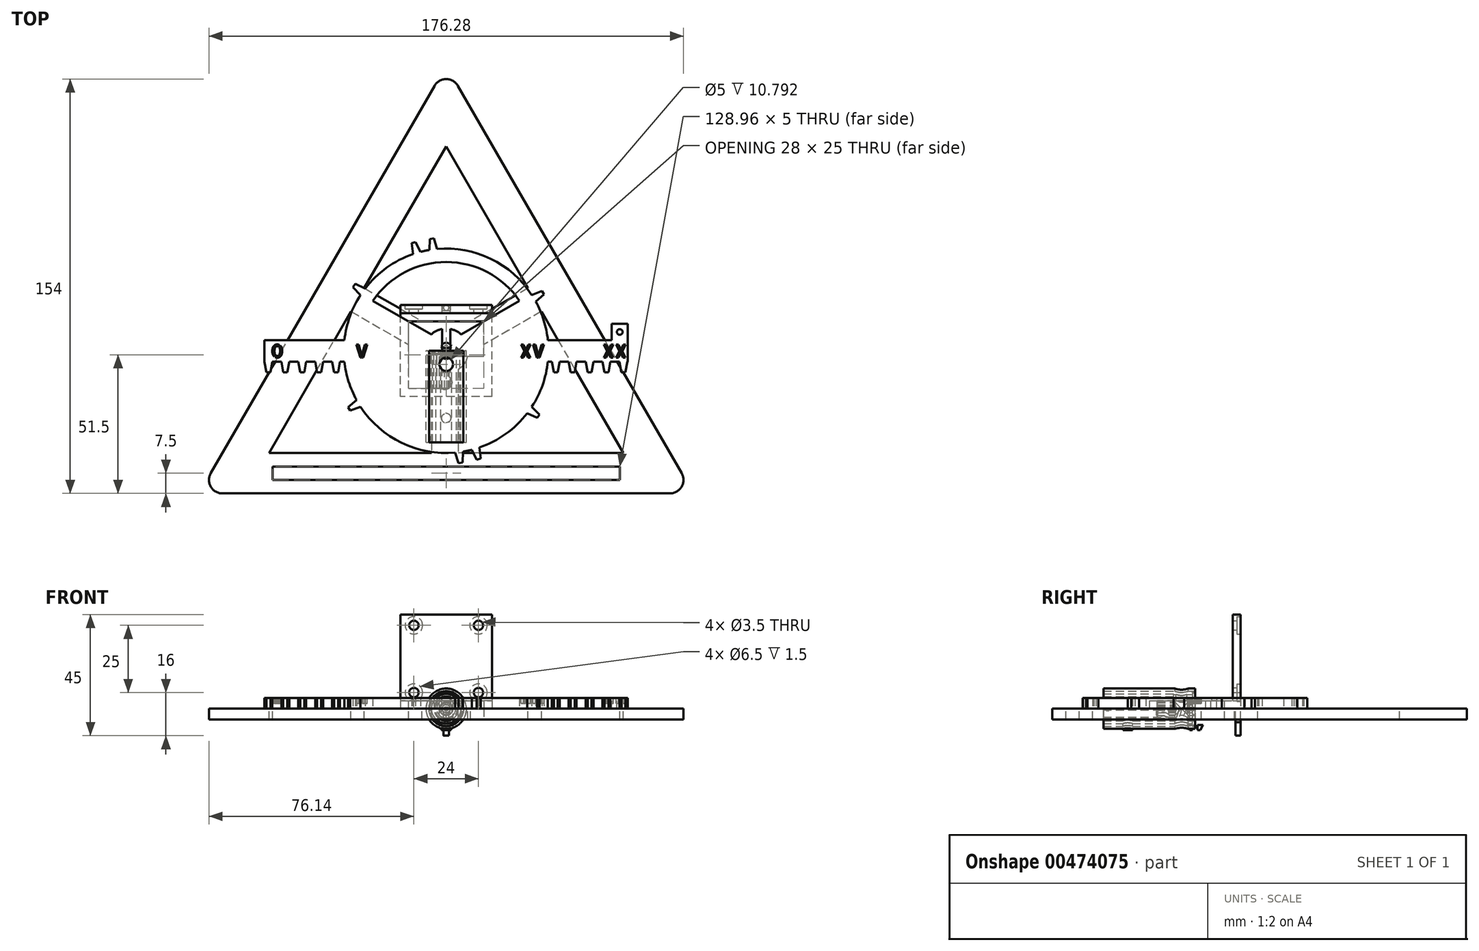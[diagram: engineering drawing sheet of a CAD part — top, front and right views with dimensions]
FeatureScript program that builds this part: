
annotation { "Feature Type Name" : "Feature", "Feature Type Description" : "" }
export const myFeature = defineFeature(function(context is Context, id is Id, definition is map)
    precondition{}
    {
        {
            var Q0;
            Q0=qCreatedBy(makeId("Top.planeOp"),FACE);
            var sketch = newSketch(context, id + "F0", { "sketchPlane" : qUnion([Q0])});
            skCircle(sketch, "E0.cCircle", {"center": v(0, 0) * mm, "radius": 53 * mm, "construction": true});
            skLineSegment(sketch, "E0.0", {"start": v(0, 106) * mm, "end": v(91.8, -53) * mm});
            skLineSegment(sketch, "E0.1", {"start": v(91.8, -53) * mm, "end": v(-91.8, -53) * mm});
            skLineSegment(sketch, "E0.2", {"start": v(-91.8, -53) * mm, "end": v(0, 106) * mm});
            skLineSegment(sketch, "E1.0", {"start": v(-83.14, -48) * mm, "end": v(0, 96) * mm});
            skLineSegment(sketch, "E1.1", {"start": v(83.14, -48) * mm, "end": v(-83.14, -48) * mm});
            skLineSegment(sketch, "E1.2", {"start": v(0, 96) * mm, "end": v(83.14, -48) * mm});
            skLineSegment(sketch, "E2.0", {"start": v(-74.48, -43) * mm, "end": v(0, 86) * mm});
            skLineSegment(sketch, "E2.1", {"start": v(74.48, -43) * mm, "end": v(-74.48, -43) * mm});
            skLineSegment(sketch, "E2.2", {"start": v(0, 86) * mm, "end": v(74.48, -43) * mm});
            skLineSegment(sketch, "E3.left", {"start": v(-64.48, -43) * mm, "end": v(-64.48, -48) * mm});
            skLineSegment(sketch, "E3.right", {"start": v(64.48, -48) * mm, "end": v(64.48, -50) * mm});
            skLineSegment(sketch, "E4", {"start": v(-69.48, -34.34) * mm, "end": v(-73.8, -31.84) * mm});
            skLineSegment(sketch, "E5", {"start": v(-5, 77.34) * mm, "end": v(-9.33, 79.84) * mm});
            skLineSegment(sketch, "E6", {"start": v(5.77, 76) * mm, "end": v(10.1, 78.5) * mm});
            skLineSegment(sketch, "E7", {"start": v(68.7, -33) * mm, "end": v(73.03, -30.5) * mm});
            skLineSegment(sketch, "E8", {"start": v(-37.24, 21.5) * mm, "end": v(-0.48, 0.28) * mm, "construction": true});
            skLineSegment(sketch, "E9", {"start": v(37.24, 21.5) * mm, "end": v(0, 0) * mm});
            skLineSegment(sketch, "E10", {"start": v(-0.48, 0.28) * mm, "end": v(-0.48, -43.46) * mm, "construction": true});
            skLineSegment(sketch, "E11.0", {"start": v(-5.48, -0.46) * mm, "end": v(-5.48, -43.46) * mm});
            skLineSegment(sketch, "E12.0", {"start": v(4.52, -0.46) * mm, "end": v(4.52, -43) * mm});
            skLineSegment(sketch, "E13.0", {"start": v(39.74, 17.17) * mm, "end": v(2.5, -4.33) * mm});
            skLineSegment(sketch, "E14.0", {"start": v(-39.74, 17.17) * mm, "end": v(-2.5, -4.33) * mm});
            skLineSegment(sketch, "E15.0", {"start": v(-34.74, 25.83) * mm, "end": v(2.5, 4.33) * mm});
            skLineSegment(sketch, "E16.0", {"start": v(65.82, -38) * mm, "end": v(-65.82, -38) * mm});
            skLineSegment(sketch, "E16.1", {"start": v(0, 76) * mm, "end": v(65.82, -38) * mm});
            skLineSegment(sketch, "E16.2", {"start": v(-65.82, -38) * mm, "end": v(0, 76) * mm});
            skLineSegment(sketch, "E17", {"start": v(64.48, -50) * mm, "end": v(64.48, -43) * mm});
            skCircle(sketch, "E18", {"center": v(10.14, 5.86) * mm, "radius": 2.6 * mm});
            skCircle(sketch, "E19", {"center": v(-10.87, 6.28) * mm, "radius": 2.6 * mm});
            skCircle(sketch, "E20", {"center": v(-0.48, -11.72) * mm, "radius": 2.6 * mm});
            skCircle(sketch, "E21", {"center": v(0, 0) * mm, "radius": 3.25 * mm});
            skPoint(sketch, "E22", {"position": v(8.18, -1.05) * mm});
            skPoint(sketch, "E23", {"position": v(4.52, -6.9) * mm});
            skPoint(sketch, "E24", {"position": v(2.67, 7.8) * mm});
            skPoint(sketch, "E25", {"position": v(-3.18, 7.61) * mm});
            skPoint(sketch, "E26", {"position": v(-8.18, -1.05) * mm});
            skPoint(sketch, "E27", {"position": v(-5.48, -6.9) * mm});
            skArc(sketch, "E28", {"start": v(8.18, -1.05) * mm, "mid": v(5.21, 6.4) * mm, "end": v(-2.68, 7.8) * mm});
            skArc(sketch, "E29", {"start": v(4.52, -6.9) * mm, "mid": v(7, -4.38) * mm, "end": v(8.18, -1.05) * mm});
            skArc(sketch, "E30", {"start": v(-2.68, 7.8) * mm, "mid": v(-7, 4.35) * mm, "end": v(-8.18, -1.05) * mm});
            skArc(sketch, "E31", {"start": v(-8.18, -1.05) * mm, "mid": v(-7.3, -3.85) * mm, "end": v(-5.48, -6.16) * mm});
            skArc(sketch, "E32", {"start": v(-5.48, -6.16) * mm, "mid": v(-0.6, -8.23) * mm, "end": v(4.52, -6.9) * mm});
            skLineSegment(sketch, "E33.0", {"start": v(34.74, 25.83) * mm, "end": v(-2.5, 4.33) * mm});
            skSolve(sketch);
        }
        {
            var Q0;
            {var subQ0=sQuery(id+"F0.wireOp",EDGE,"E2.2");var subQ1=sQuery(id+"F0.wireOp",EDGE,"E2.1");var subQ2=makeQuery(id+"F0.imprint","INTERSECT",VERTEX,{"derivedFrom":[subQ1,subQ0]});Q0=makeQuery(id+"F0.imprint","IMPRINT",FACE,{"disambiguationData":[TD([[makeQuery(id+"F0.imprint","IMPRINT",EDGE,{"disambiguationData":[TD([[subQ2,-1.0]])],"derivedFrom":subQ1}),-1.0]])]});}
            var Q1;
            Q1=makeQuery(id+"F0.imprint","IMPRINT",FACE,{"disambiguationData":[TD([[makeQuery(id+"F0.imprint","IMPRINT",EDGE,{"derivedFrom":sQuery(id+"F0.wireOp",EDGE,"E0.0")}),-1.0]])]});
            var Q2;
            {var subQ4=sQuery(id+"F0.wireOp",EDGE,"E2.0");var subQ6=makeQuery(id+"F0.imprint","INTERSECT",VERTEX,{"derivedFrom":[subQ4,sQuery(id+"F0.wireOp",EDGE,"E5")]});Q2=makeQuery(id+"F0.imprint","IMPRINT",FACE,{"disambiguationData":[TD([[makeQuery(id+"F0.imprint","IMPRINT",EDGE,{"disambiguationData":[TD([[subQ6,1.0]])],"derivedFrom":subQ4}),-1.0]])]});}
            var Q3;
            {var subQ0=sQuery(id+"F0.wireOp",EDGE,"E2.1");var subQ1=sQuery(id+"F0.wireOp",EDGE,"E2.0");var subQ2=makeQuery(id+"F0.imprint","INTERSECT",VERTEX,{"derivedFrom":[subQ1,subQ0]});Q3=makeQuery(id+"F0.imprint","IMPRINT",FACE,{"disambiguationData":[TD([[makeQuery(id+"F0.imprint","IMPRINT",EDGE,{"disambiguationData":[TD([[subQ2,-1.0]])],"derivedFrom":subQ1}),-1.0]])]});}
            var Q4;
            {var subQ0=sQuery(id+"F0.wireOp",EDGE,"6e593ad5-b7bf-4e4b-92ed-28ec4f3bcc03.0");var subQ1=sQuery(id+"F0.wireOp",EDGE,"E11.0");var subQ2=makeQuery(id+"F0.imprint","INTERSECT",VERTEX,{"derivedFrom":[subQ1,subQ0]});Q4=makeQuery(id+"F0.imprint","IMPRINT",FACE,{"disambiguationData":[TD([[makeQuery(id+"F0.imprint","IMPRINT",EDGE,{"disambiguationData":[TD([[subQ2,-1.0]])],"derivedFrom":subQ1}),1.0]])]});}
            var Q5;
            {var subQ0=sQuery(id+"F0.wireOp",EDGE,"E16.1");var subQ1=sQuery(id+"F0.wireOp",EDGE,"7c9a6aae-f412-4e27-b171-df1cd759398a.0");var subQ2=makeQuery(id+"F0.imprint","INTERSECT",VERTEX,{"derivedFrom":[subQ1,subQ0]});Q5=makeQuery(id+"F0.imprint","IMPRINT",FACE,{"disambiguationData":[TD([[makeQuery(id+"F0.imprint","IMPRINT",EDGE,{"disambiguationData":[TD([[subQ2,-1.0]])],"derivedFrom":subQ1}),1.0]])]});}
            var Q6;
            {var subQ0=sQuery(id+"F0.wireOp",EDGE,"7c9a6aae-f412-4e27-b171-df1cd759398a.0");var subQ1=sQuery(id+"F0.wireOp",EDGE,"E2.2");var subQ2=makeQuery(id+"F0.imprint","INTERSECT",VERTEX,{"derivedFrom":[subQ1,subQ0]});Q6=makeQuery(id+"F0.imprint","IMPRINT",FACE,{"disambiguationData":[TD([[makeQuery(id+"F0.imprint","IMPRINT",EDGE,{"disambiguationData":[TD([[subQ2,-1.0]])],"derivedFrom":subQ1}),-1.0]])]});}
            var Q7;
            {var subQ0=sQuery(id+"F0.wireOp",EDGE,"E16.2");var subQ1=sQuery(id+"F0.wireOp",EDGE,"E14.0");var subQ2=makeQuery(id+"F0.imprint","INTERSECT",VERTEX,{"derivedFrom":[subQ1,subQ0]});Q7=makeQuery(id+"F0.imprint","IMPRINT",FACE,{"disambiguationData":[TD([[makeQuery(id+"F0.imprint","IMPRINT",EDGE,{"disambiguationData":[TD([[subQ2,-1.0]])],"derivedFrom":subQ1}),1.0]])]});}
            var Q8;
            {var subQ3=sQuery(id+"F0.wireOp",EDGE,"E3.left");Q8=makeQuery(id+"F0.imprint","IMPRINT",FACE,{"disambiguationData":[TD([[makeQuery(id+"F0.imprint","IMPRINT",EDGE,{"derivedFrom":subQ3}),-1.0]])]});}
            var Q9;
            {var subQ0=sQuery(id+"F0.wireOp",EDGE,"E11.0");var subQ1=sQuery(id+"F0.wireOp",EDGE,"E2.1");var subQ2=makeQuery(id+"F0.imprint","INTERSECT",VERTEX,{"derivedFrom":[subQ1,subQ0]});Q9=makeQuery(id+"F0.imprint","IMPRINT",FACE,{"disambiguationData":[TD([[makeQuery(id+"F0.imprint","IMPRINT",EDGE,{"disambiguationData":[TD([[subQ2,1.0]])],"derivedFrom":subQ1}),-1.0]])]});}
            var Q10;
            {var subQ3=sQuery(id+"F0.wireOp",EDGE,"E3.right");Q10=makeQuery(id+"F0.imprint","IMPRINT",FACE,{"disambiguationData":[TD([[makeQuery(id+"F0.imprint","IMPRINT",EDGE,{"derivedFrom":subQ3}),1.0]])]});}
            var Q11;
            {var subQ0=sQuery(id+"F0.wireOp",EDGE,"E14.0");var subQ1=sQuery(id+"F0.wireOp",EDGE,"E2.0");var subQ2=makeQuery(id+"F0.imprint","INTERSECT",VERTEX,{"derivedFrom":[subQ1,subQ0]});Q11=makeQuery(id+"F0.imprint","IMPRINT",FACE,{"disambiguationData":[TD([[makeQuery(id+"F0.imprint","IMPRINT",EDGE,{"disambiguationData":[TD([[subQ2,-1.0]])],"derivedFrom":subQ1}),-1.0]])]});}
            var Q12;
            {var subQ4=sQuery(id+"F0.wireOp",EDGE,"E5");Q12=makeQuery(id+"F0.imprint","IMPRINT",FACE,{"disambiguationData":[TD([[makeQuery(id+"F0.imprint","IMPRINT",EDGE,{"derivedFrom":subQ4}),-1.0]])]});}
            var Q13;
            {var subQ0=sQuery(id+"F0.wireOp",EDGE,"FIZKjkHe-5DKq-kj0t-uyza-zxFxrPnBpY9F");var subQ1=sQuery(id+"F0.wireOp",EDGE,"E11.0");var subQ2=makeQuery(id+"F0.imprint","INTERSECT",VERTEX,{"derivedFrom":[subQ1,subQ0]});Q13=makeQuery(id+"F0.imprint","IMPRINT",FACE,{"disambiguationData":[TD([[makeQuery(id+"F0.imprint","IMPRINT",EDGE,{"disambiguationData":[TD([[subQ2,-1.0]])],"derivedFrom":subQ1}),1.0]])]});}
            var Q14;
            {var subQ0=sQuery(id+"F0.wireOp",EDGE,"FIZKjkHe-5DKq-kj0t-uyza-zxFxrPnBpY9F");var subQ1=sQuery(id+"F0.wireOp",EDGE,"E12.0");var subQ2=makeQuery(id+"F0.imprint","INTERSECT",VERTEX,{"derivedFrom":[subQ1,subQ0]});Q14=makeQuery(id+"F0.imprint","IMPRINT",FACE,{"disambiguationData":[TD([[makeQuery(id+"F0.imprint","IMPRINT",EDGE,{"disambiguationData":[TD([[subQ2,-1.0]])],"derivedFrom":subQ1}),1.0]])]});}
            var Q15;
            {var subQ0=sQuery(id+"F0.wireOp",EDGE,"FIZKjkHe-5DKq-kj0t-uyza-zxFxrPnBpY9F");var subQ1=sQuery(id+"F0.wireOp",EDGE,"E11.0");var subQ2=makeQuery(id+"F0.imprint","INTERSECT",VERTEX,{"derivedFrom":[subQ1,subQ0]});Q15=makeQuery(id+"F0.imprint","IMPRINT",FACE,{"disambiguationData":[TD([[makeQuery(id+"F0.imprint","IMPRINT",EDGE,{"disambiguationData":[TD([[subQ2,-1.0]])],"derivedFrom":subQ1}),-1.0]])]});}
            var Q16;
            {var subQ0=sQuery(id+"F0.wireOp",EDGE,"FIZKjkHe-5DKq-kj0t-uyza-zxFxrPnBpY9F");var subQ1=sQuery(id+"F0.wireOp",EDGE,"7c9a6aae-f412-4e27-b171-df1cd759398a.0");var subQ2=makeQuery(id+"F0.imprint","INTERSECT",VERTEX,{"derivedFrom":[subQ1,subQ0]});Q16=makeQuery(id+"F0.imprint","IMPRINT",FACE,{"disambiguationData":[TD([[makeQuery(id+"F0.imprint","IMPRINT",EDGE,{"disambiguationData":[TD([[subQ2,1.0]])],"derivedFrom":subQ1}),1.0]])]});}
            var Q17;
            {var subQ7=sQuery(id+"F0.wireOp",EDGE,"E7");Q17=makeQuery(id+"F0.imprint","IMPRINT",FACE,{"disambiguationData":[TD([[makeQuery(id+"F0.imprint","IMPRINT",EDGE,{"derivedFrom":subQ7}),-1.0]])]});}
            var Q18;
            {var subQ0=sQuery(id+"F0.wireOp",EDGE,"E14.0");var subQ1=sQuery(id+"F0.wireOp",EDGE,"E11.0");var subQ2=makeQuery(id+"F0.imprint","INTERSECT",VERTEX,{"derivedFrom":[subQ1,subQ0]});Q18=makeQuery(id+"F0.imprint","IMPRINT",FACE,{"disambiguationData":[TD([[makeQuery(id+"F0.imprint","IMPRINT",EDGE,{"disambiguationData":[TD([[subQ2,-1.0]])],"derivedFrom":subQ1}),-1.0]])]});}
            var Q19;
            {var subQ1=sQuery(id+"F0.wireOp",EDGE,"E14.0");var subQ3=sQuery(id+"F0.wireOp",EDGE,"E11.0");var subQ4=makeQuery(id+"F0.imprint","INTERSECT",VERTEX,{"derivedFrom":[subQ3,subQ1]});Q19=makeQuery(id+"F0.imprint","IMPRINT",FACE,{"disambiguationData":[TD([[makeQuery(id+"F0.imprint","IMPRINT",EDGE,{"disambiguationData":[TD([[subQ4,-1.0]])],"derivedFrom":subQ3}),1.0]])]});}
            var Q20;
            {var subQ0=sQuery(id+"F0.wireOp",EDGE,"E13.0");var subQ1=sQuery(id+"F0.wireOp",EDGE,"E12.0");var subQ2=makeQuery(id+"F0.imprint","INTERSECT",VERTEX,{"derivedFrom":[subQ1,subQ0]});Q20=makeQuery(id+"F0.imprint","IMPRINT",FACE,{"disambiguationData":[TD([[makeQuery(id+"F0.imprint","IMPRINT",EDGE,{"disambiguationData":[TD([[subQ2,-1.0]])],"derivedFrom":subQ1}),1.0]])]});}
            var Q21;
            {var subQ0=sQuery(id+"F0.wireOp",EDGE,"6e593ad5-b7bf-4e4b-92ed-28ec4f3bcc03.0");var subQ1=sQuery(id+"F0.wireOp",EDGE,"7c9a6aae-f412-4e27-b171-df1cd759398a.0");var subQ2=makeQuery(id+"F0.imprint","INTERSECT",VERTEX,{"derivedFrom":[subQ1,subQ0]});Q21=makeQuery(id+"F0.imprint","IMPRINT",FACE,{"disambiguationData":[TD([[makeQuery(id+"F0.imprint","IMPRINT",EDGE,{"disambiguationData":[TD([[subQ2,-1.0]])],"derivedFrom":subQ1}),-1.0]])]});}
            var Q22;
            {var subQ1=sQuery(id+"F0.wireOp",EDGE,"7c9a6aae-f412-4e27-b171-df1cd759398a.0");var subQ5=sQuery(id+"F0.wireOp",EDGE,"FIZKjkHe-5DKq-kj0t-uyza-zxFxrPnBpY9F");var subQ6=makeQuery(id+"F0.imprint","INTERSECT",VERTEX,{"derivedFrom":[subQ1,subQ5]});Q22=makeQuery(id+"F0.imprint","IMPRINT",FACE,{"disambiguationData":[TD([[makeQuery(id+"F0.imprint","IMPRINT",EDGE,{"disambiguationData":[TD([[subQ6,1.0]])],"derivedFrom":subQ1}),-1.0]])]});}
            var Q23;
            {var subQ1=sQuery(id+"F0.wireOp",EDGE,"E9");var subQ4=sQuery(id+"F0.wireOp",EDGE,"E16.1");var subQ5=makeQuery(id+"F0.imprint","INTERSECT",VERTEX,{"derivedFrom":[subQ1,subQ4]});Q23=makeQuery(id+"F0.imprint","IMPRINT",FACE,{"disambiguationData":[TD([[makeQuery(id+"F0.imprint","IMPRINT",EDGE,{"disambiguationData":[TD([[subQ5,-1.0]])],"derivedFrom":subQ1}),-1.0]])]});}
            var Q24;
            {var subQ3=sQuery(id+"F0.wireOp",EDGE,"E16.1");var subQ5=sQuery(id+"F0.wireOp",EDGE,"E9");var subQ6=makeQuery(id+"F0.imprint","INTERSECT",VERTEX,{"derivedFrom":[subQ5,subQ3]});Q24=makeQuery(id+"F0.imprint","IMPRINT",FACE,{"disambiguationData":[TD([[makeQuery(id+"F0.imprint","IMPRINT",EDGE,{"disambiguationData":[TD([[subQ6,-1.0]])],"derivedFrom":subQ5}),1.0]])]});}
            var Q25;
            {var subQ0=sQuery(id+"F0.wireOp",EDGE,"E9");var subQ1=sQuery(id+"F0.wireOp",EDGE,"E2.2");var subQ2=makeQuery(id+"F0.imprint","INTERSECT",VERTEX,{"derivedFrom":[subQ1,subQ0]});Q25=makeQuery(id+"F0.imprint","IMPRINT",FACE,{"disambiguationData":[TD([[makeQuery(id+"F0.imprint","IMPRINT",EDGE,{"disambiguationData":[TD([[subQ2,-1.0]])],"derivedFrom":subQ1}),-1.0]])]});}
            var Q26;
            {var subQ0=sQuery(id+"F0.wireOp",EDGE,"E9");var subQ1=sQuery(id+"F0.wireOp",EDGE,"E2.2");var subQ2=makeQuery(id+"F0.imprint","INTERSECT",VERTEX,{"derivedFrom":[subQ1,subQ0]});Q26=makeQuery(id+"F0.imprint","IMPRINT",FACE,{"disambiguationData":[TD([[makeQuery(id+"F0.imprint","IMPRINT",EDGE,{"disambiguationData":[TD([[subQ2,1.0]])],"derivedFrom":subQ1}),-1.0]])]});}
            var Q27;
            Q27=makeQuery(id+"F0.imprint","IMPRINT",FACE,{"disambiguationData":[TD([[makeQuery(id+"F0.imprint","IMPRINT",EDGE,{"derivedFrom":sQuery(id+"F0.wireOp",EDGE,"E20")}),-1.0]])]});
            var Q28;
            {var subQ0=sQuery(id+"F0.wireOp",EDGE,"E33.0");var subQ1=sQuery(id+"F0.wireOp",EDGE,"E15.0");var subQ2=makeQuery(id+"F0.imprint","INTERSECT",VERTEX,{"derivedFrom":[subQ1,subQ0]});Q28=makeQuery(id+"F0.imprint","IMPRINT",FACE,{"disambiguationData":[TD([[makeQuery(id+"F0.imprint","IMPRINT",EDGE,{"disambiguationData":[TD([[subQ2,1.0]])],"derivedFrom":subQ1}),1.0]])]});}
            extrude(context, id + "F1", {"entities" : qUnion([Q0, Q1, Q2, Q3, Q4, Q5, Q6, Q7, Q8, Q9, Q10, Q11, Q12, Q13, Q14, Q15, Q16, Q17, Q18, Q19, Q20, Q21, Q22, Q23, Q24, Q25, Q26, Q27, Q28]), "oppositeDirection" : true, "depth" : 4 * mm, "offsetDistance" : 25 * mm});
        }
        {
            var Q0;
            Q0=qCreatedBy(makeId("Top.planeOp"),FACE);
            var sketch = newSketch(context, id + "F2", { "sketchPlane" : qUnion([Q0])});
            skLineSegment(sketch, "E34.bottom", {"start": v(67.5, -4) * mm, "end": v(-67.5, -4) * mm});
            skLineSegment(sketch, "E34.top", {"start": v(67.5, 4) * mm, "end": v(-67.5, 4) * mm});
            skLineSegment(sketch, "E34.left", {"start": v(67.5, -4) * mm, "end": v(67.5, 4) * mm});
            skLineSegment(sketch, "E34.right", {"start": v(-67.5, -4) * mm, "end": v(-67.5, 4) * mm});
            skCircle(sketch, "E35", {"center": v(0, 0) * mm, "radius": 2.25 * mm});
            skLineSegment(sketch, "E36", {"start": v(-67.5, -4) * mm, "end": v(-66.8, -8) * mm});
            skLineSegment(sketch, "E37", {"start": v(-66.8, -8) * mm, "end": v(-65.3, -8) * mm});
            skLineSegment(sketch, "E38", {"start": v(-65.3, -8) * mm, "end": v(-64.59, -4) * mm});
            skLineSegment(sketch, "E39.1.0.0", {"start": v(-61.22, -4) * mm, "end": v(-60.51, -8) * mm});
            skLineSegment(sketch, "E39.1.0.1", {"start": v(-59.01, -8) * mm, "end": v(-58.3, -4) * mm});
            skLineSegment(sketch, "E39.1.0.2", {"start": v(-60.51, -8) * mm, "end": v(-59.01, -8) * mm});
            skLineSegment(sketch, "E39.2.0.0", {"start": v(-54.94, -4) * mm, "end": v(-54.23, -8) * mm});
            skLineSegment(sketch, "E39.2.0.1", {"start": v(-52.73, -8) * mm, "end": v(-52.03, -4) * mm});
            skLineSegment(sketch, "E39.2.0.2", {"start": v(-54.23, -8) * mm, "end": v(-52.73, -8) * mm});
            skLineSegment(sketch, "E39.3.0.0", {"start": v(-48.66, -4) * mm, "end": v(-47.95, -8) * mm});
            skLineSegment(sketch, "E39.3.0.1", {"start": v(-46.45, -8) * mm, "end": v(-45.75, -4) * mm});
            skLineSegment(sketch, "E39.3.0.2", {"start": v(-47.95, -8) * mm, "end": v(-46.45, -8) * mm});
            skLineSegment(sketch, "E39.4.0.0", {"start": v(-42.38, -4) * mm, "end": v(-41.67, -8) * mm});
            skLineSegment(sketch, "E39.4.0.1", {"start": v(-40.17, -8) * mm, "end": v(-39.47, -4) * mm});
            skLineSegment(sketch, "E39.4.0.2", {"start": v(-41.67, -8) * mm, "end": v(-40.17, -8) * mm});
            skLineSegment(sketch, "E39.5.0.0", {"start": v(-36.1, -4) * mm, "end": v(-35.4, -8) * mm});
            skLineSegment(sketch, "E39.5.0.1", {"start": v(-33.9, -8) * mm, "end": v(-33.19, -4) * mm});
            skLineSegment(sketch, "E39.5.0.2", {"start": v(-35.4, -8) * mm, "end": v(-33.9, -8) * mm});
            skLineSegment(sketch, "E39.6.0.0", {"start": v(-29.82, -4) * mm, "end": v(-29.11, -8) * mm});
            skLineSegment(sketch, "E39.6.0.1", {"start": v(-27.61, -8) * mm, "end": v(-26.9, -4) * mm});
            skLineSegment(sketch, "E39.6.0.2", {"start": v(-29.11, -8) * mm, "end": v(-27.61, -8) * mm});
            skLineSegment(sketch, "E39.7.0.0", {"start": v(-23.54, -4) * mm, "end": v(-22.83, -8) * mm});
            skLineSegment(sketch, "E39.7.0.1", {"start": v(-21.33, -8) * mm, "end": v(-20.63, -4) * mm});
            skLineSegment(sketch, "E39.7.0.2", {"start": v(-22.83, -8) * mm, "end": v(-21.33, -8) * mm});
            skLineSegment(sketch, "E39.8.0.0", {"start": v(-17.26, -4) * mm, "end": v(-16.55, -8) * mm});
            skLineSegment(sketch, "E39.8.0.1", {"start": v(-15.05, -8) * mm, "end": v(-14.35, -4) * mm});
            skLineSegment(sketch, "E39.8.0.2", {"start": v(-16.55, -8) * mm, "end": v(-15.05, -8) * mm});
            skLineSegment(sketch, "E39.9.0.0", {"start": v(-10.98, -4) * mm, "end": v(-10.27, -8) * mm});
            skLineSegment(sketch, "E39.9.0.1", {"start": v(-8.77, -8) * mm, "end": v(-8.07, -4) * mm});
            skLineSegment(sketch, "E39.9.0.2", {"start": v(-10.27, -8) * mm, "end": v(-8.77, -8) * mm});
            skLineSegment(sketch, "E39.10.0.0", {"start": v(-4.7, -4) * mm, "end": v(-4, -8) * mm});
            skLineSegment(sketch, "E39.10.0.1", {"start": v(-2.5, -8) * mm, "end": v(-1.79, -4) * mm});
            skLineSegment(sketch, "E39.10.0.2", {"start": v(-4, -8) * mm, "end": v(-2.5, -8) * mm});
            skLineSegment(sketch, "E39.11.0.0", {"start": v(1.58, -4) * mm, "end": v(2.29, -8) * mm});
            skLineSegment(sketch, "E39.11.0.1", {"start": v(3.79, -8) * mm, "end": v(4.5, -4) * mm});
            skLineSegment(sketch, "E39.11.0.2", {"start": v(2.29, -8) * mm, "end": v(3.79, -8) * mm});
            skLineSegment(sketch, "E39.12.0.0", {"start": v(7.86, -4) * mm, "end": v(8.57, -8) * mm});
            skLineSegment(sketch, "E39.12.0.1", {"start": v(10.07, -8) * mm, "end": v(10.77, -4) * mm});
            skLineSegment(sketch, "E39.12.0.2", {"start": v(8.57, -8) * mm, "end": v(10.07, -8) * mm});
            skLineSegment(sketch, "E39.13.0.0", {"start": v(14.14, -4) * mm, "end": v(14.85, -8) * mm});
            skLineSegment(sketch, "E39.13.0.1", {"start": v(16.35, -8) * mm, "end": v(17.05, -4) * mm});
            skLineSegment(sketch, "E39.13.0.2", {"start": v(14.85, -8) * mm, "end": v(16.35, -8) * mm});
            skLineSegment(sketch, "E39.14.0.0", {"start": v(20.42, -4) * mm, "end": v(21.13, -8) * mm});
            skLineSegment(sketch, "E39.14.0.1", {"start": v(22.63, -8) * mm, "end": v(23.33, -4) * mm});
            skLineSegment(sketch, "E39.14.0.2", {"start": v(21.13, -8) * mm, "end": v(22.63, -8) * mm});
            skLineSegment(sketch, "E39.15.0.0", {"start": v(26.7, -4) * mm, "end": v(27.4, -8) * mm});
            skLineSegment(sketch, "E39.15.0.1", {"start": v(28.9, -8) * mm, "end": v(29.61, -4) * mm});
            skLineSegment(sketch, "E39.15.0.2", {"start": v(27.4, -8) * mm, "end": v(28.9, -8) * mm});
            skLineSegment(sketch, "E39.16.0.0", {"start": v(32.98, -4) * mm, "end": v(33.69, -8) * mm});
            skLineSegment(sketch, "E39.16.0.1", {"start": v(35.19, -8) * mm, "end": v(35.9, -4) * mm});
            skLineSegment(sketch, "E39.16.0.2", {"start": v(33.69, -8) * mm, "end": v(35.19, -8) * mm});
            skLineSegment(sketch, "E39.17.0.0", {"start": v(39.26, -4) * mm, "end": v(39.97, -8) * mm});
            skLineSegment(sketch, "E39.17.0.1", {"start": v(41.47, -8) * mm, "end": v(42.17, -4) * mm});
            skLineSegment(sketch, "E39.17.0.2", {"start": v(39.97, -8) * mm, "end": v(41.47, -8) * mm});
            skLineSegment(sketch, "E39.18.0.0", {"start": v(45.54, -4) * mm, "end": v(46.25, -8) * mm});
            skLineSegment(sketch, "E39.18.0.1", {"start": v(47.75, -8) * mm, "end": v(48.45, -4) * mm});
            skLineSegment(sketch, "E39.18.0.2", {"start": v(46.25, -8) * mm, "end": v(47.75, -8) * mm});
            skLineSegment(sketch, "E39.19.0.0", {"start": v(51.82, -4) * mm, "end": v(52.53, -8) * mm});
            skLineSegment(sketch, "E39.19.0.1", {"start": v(54.03, -8) * mm, "end": v(54.73, -4) * mm});
            skLineSegment(sketch, "E39.19.0.2", {"start": v(52.53, -8) * mm, "end": v(54.03, -8) * mm});
            skLineSegment(sketch, "E39.direction1", {"start": v(-66.8, -8) * mm, "end": v(-60.51, -8) * mm, "construction": true});
            skLineSegment(sketch, "E40.0.20.0", {"start": v(58.1, -4) * mm, "end": v(58.8, -8) * mm});
            skLineSegment(sketch, "E40.3.20.0", {"start": v(60.3, -8) * mm, "end": v(61.01, -4) * mm});
            skLineSegment(sketch, "E40.6.20.0", {"start": v(58.8, -8) * mm, "end": v(60.3, -8) * mm});
            skLineSegment(sketch, "E40.0.21.0", {"start": v(64.38, -4) * mm, "end": v(65.09, -8) * mm});
            skLineSegment(sketch, "E40.3.21.0", {"start": v(66.59, -8) * mm, "end": v(67.3, -4) * mm});
            skLineSegment(sketch, "E40.6.21.0", {"start": v(65.09, -8) * mm, "end": v(66.59, -8) * mm});
            skSolve(sketch);
        }
        {
            var Q0;
            Q0=makeQuery(id+"F2.imprint","IMPRINT",FACE,{"disambiguationData":[TD([[makeQuery(id+"F2.imprint","IMPRINT",EDGE,{"derivedFrom":sQuery(id+"F2.wireOp",EDGE,"E34.bottom")}),-1.0]])]});
            var Q1;
            Q1=makeQuery(id+"F2.imprint","IMPRINT",FACE,{"disambiguationData":[TD([[makeQuery(id+"F2.imprint","IMPRINT",EDGE,{"derivedFrom":sQuery(id+"F2.wireOp",EDGE,"E35")}),1.0]])]});
            var Q2;
            Q2=makeQuery(id+"F2.imprint","IMPRINT",FACE,{"disambiguationData":[TD([[makeQuery(id+"F2.imprint","IMPRINT",EDGE,{"derivedFrom":sQuery(id+"F2.wireOp",EDGE,"mbHhY8bN-gBew-p180-q6Er-AGhfJGSz6yKE.bottom")}),-1.0]])]});
            extrude(context, id + "F3", {"entities" : qUnion([Q0, Q1, Q2]), "depth" : 4 * mm, "offsetDistance" : 25 * mm});
        }
        {
            var Q0;
            Q0=makeQuery(id+"F2.imprint","IMPRINT",FACE,{"disambiguationData":[TD([[makeQuery(id+"F2.imprint","IMPRINT",EDGE,{"derivedFrom":sQuery(id+"F2.wireOp",EDGE,"E35")}),1.0]])]});
            extrude(context, id + "F4", {"entities" : qUnion([Q0]), "operationType" : NewBodyOperationType.ADD, "oppositeDirection" : true, "depth" : 6 * mm, "offsetDistance" : 25 * mm});
        }
        {
            var Q0;
            {var subQ0=sQuery(id+"F2.wireOp",EDGE,"E36");Q0=makeQuery(id+"F2.imprint","IMPRINT",FACE,{"disambiguationData":[TD([[makeQuery(id+"F2.imprint","IMPRINT",EDGE,{"derivedFrom":subQ0}),1.0]])]});}
            var Q1;
            {var subQ0=sQuery(id+"F2.wireOp",EDGE,"E39.1.0.0");Q1=makeQuery(id+"F2.imprint","IMPRINT",FACE,{"disambiguationData":[TD([[makeQuery(id+"F2.imprint","IMPRINT",EDGE,{"derivedFrom":subQ0}),1.0]])]});}
            var Q2;
            {var subQ0=sQuery(id+"F2.wireOp",EDGE,"E39.2.0.0");Q2=makeQuery(id+"F2.imprint","IMPRINT",FACE,{"disambiguationData":[TD([[makeQuery(id+"F2.imprint","IMPRINT",EDGE,{"derivedFrom":subQ0}),1.0]])]});}
            var Q3;
            {var subQ0=sQuery(id+"F2.wireOp",EDGE,"E39.3.0.0");Q3=makeQuery(id+"F2.imprint","IMPRINT",FACE,{"disambiguationData":[TD([[makeQuery(id+"F2.imprint","IMPRINT",EDGE,{"derivedFrom":subQ0}),1.0]])]});}
            var Q4;
            {var subQ0=sQuery(id+"F2.wireOp",EDGE,"E39.4.0.0");Q4=makeQuery(id+"F2.imprint","IMPRINT",FACE,{"disambiguationData":[TD([[makeQuery(id+"F2.imprint","IMPRINT",EDGE,{"derivedFrom":subQ0}),1.0]])]});}
            var Q5;
            {var subQ0=sQuery(id+"F2.wireOp",EDGE,"E39.5.0.0");Q5=makeQuery(id+"F2.imprint","IMPRINT",FACE,{"disambiguationData":[TD([[makeQuery(id+"F2.imprint","IMPRINT",EDGE,{"derivedFrom":subQ0}),1.0]])]});}
            var Q6;
            {var subQ0=sQuery(id+"F2.wireOp",EDGE,"E39.6.0.0");Q6=makeQuery(id+"F2.imprint","IMPRINT",FACE,{"disambiguationData":[TD([[makeQuery(id+"F2.imprint","IMPRINT",EDGE,{"derivedFrom":subQ0}),1.0]])]});}
            var Q7;
            {var subQ0=sQuery(id+"F2.wireOp",EDGE,"E39.7.0.0");Q7=makeQuery(id+"F2.imprint","IMPRINT",FACE,{"disambiguationData":[TD([[makeQuery(id+"F2.imprint","IMPRINT",EDGE,{"derivedFrom":subQ0}),1.0]])]});}
            var Q8;
            {var subQ0=sQuery(id+"F2.wireOp",EDGE,"E39.8.0.0");Q8=makeQuery(id+"F2.imprint","IMPRINT",FACE,{"disambiguationData":[TD([[makeQuery(id+"F2.imprint","IMPRINT",EDGE,{"derivedFrom":subQ0}),1.0]])]});}
            var Q9;
            {var subQ0=sQuery(id+"F2.wireOp",EDGE,"E39.9.0.0");Q9=makeQuery(id+"F2.imprint","IMPRINT",FACE,{"disambiguationData":[TD([[makeQuery(id+"F2.imprint","IMPRINT",EDGE,{"derivedFrom":subQ0}),1.0]])]});}
            var Q10;
            {var subQ0=sQuery(id+"F2.wireOp",EDGE,"E39.10.0.0");Q10=makeQuery(id+"F2.imprint","IMPRINT",FACE,{"disambiguationData":[TD([[makeQuery(id+"F2.imprint","IMPRINT",EDGE,{"derivedFrom":subQ0}),1.0]])]});}
            var Q11;
            {var subQ0=sQuery(id+"F2.wireOp",EDGE,"E39.11.0.0");Q11=makeQuery(id+"F2.imprint","IMPRINT",FACE,{"disambiguationData":[TD([[makeQuery(id+"F2.imprint","IMPRINT",EDGE,{"derivedFrom":subQ0}),1.0]])]});}
            var Q12;
            {var subQ0=sQuery(id+"F2.wireOp",EDGE,"E39.12.0.0");Q12=makeQuery(id+"F2.imprint","IMPRINT",FACE,{"disambiguationData":[TD([[makeQuery(id+"F2.imprint","IMPRINT",EDGE,{"derivedFrom":subQ0}),1.0]])]});}
            var Q13;
            {var subQ0=sQuery(id+"F2.wireOp",EDGE,"E39.13.0.0");Q13=makeQuery(id+"F2.imprint","IMPRINT",FACE,{"disambiguationData":[TD([[makeQuery(id+"F2.imprint","IMPRINT",EDGE,{"derivedFrom":subQ0}),1.0]])]});}
            var Q14;
            {var subQ0=sQuery(id+"F2.wireOp",EDGE,"E39.14.0.0");Q14=makeQuery(id+"F2.imprint","IMPRINT",FACE,{"disambiguationData":[TD([[makeQuery(id+"F2.imprint","IMPRINT",EDGE,{"derivedFrom":subQ0}),1.0]])]});}
            var Q15;
            {var subQ0=sQuery(id+"F2.wireOp",EDGE,"E39.15.0.0");Q15=makeQuery(id+"F2.imprint","IMPRINT",FACE,{"disambiguationData":[TD([[makeQuery(id+"F2.imprint","IMPRINT",EDGE,{"derivedFrom":subQ0}),1.0]])]});}
            var Q16;
            {var subQ0=sQuery(id+"F2.wireOp",EDGE,"E39.16.0.0");Q16=makeQuery(id+"F2.imprint","IMPRINT",FACE,{"disambiguationData":[TD([[makeQuery(id+"F2.imprint","IMPRINT",EDGE,{"derivedFrom":subQ0}),1.0]])]});}
            var Q17;
            {var subQ0=sQuery(id+"F2.wireOp",EDGE,"E39.17.0.0");Q17=makeQuery(id+"F2.imprint","IMPRINT",FACE,{"disambiguationData":[TD([[makeQuery(id+"F2.imprint","IMPRINT",EDGE,{"derivedFrom":subQ0}),1.0]])]});}
            var Q18;
            {var subQ0=sQuery(id+"F2.wireOp",EDGE,"E39.18.0.0");Q18=makeQuery(id+"F2.imprint","IMPRINT",FACE,{"disambiguationData":[TD([[makeQuery(id+"F2.imprint","IMPRINT",EDGE,{"derivedFrom":subQ0}),1.0]])]});}
            var Q19;
            {var subQ0=sQuery(id+"F2.wireOp",EDGE,"E39.19.0.0");Q19=makeQuery(id+"F2.imprint","IMPRINT",FACE,{"disambiguationData":[TD([[makeQuery(id+"F2.imprint","IMPRINT",EDGE,{"derivedFrom":subQ0}),1.0]])]});}
            var Q20;
            {var subQ0=sQuery(id+"F2.wireOp",EDGE,"E40.0.20.0");Q20=makeQuery(id+"F2.imprint","IMPRINT",FACE,{"disambiguationData":[TD([[makeQuery(id+"F2.imprint","IMPRINT",EDGE,{"derivedFrom":subQ0}),1.0]])]});}
            var Q21;
            {var subQ0=sQuery(id+"F2.wireOp",EDGE,"E40.0.21.0");Q21=makeQuery(id+"F2.imprint","IMPRINT",FACE,{"disambiguationData":[TD([[makeQuery(id+"F2.imprint","IMPRINT",EDGE,{"derivedFrom":subQ0}),1.0]])]});}
            var Q22;
            Q22=sQuery(id+"F2.wireOp",EDGE,"E39.11.0.0");
            var Q23;
            Q23=sQuery(id+"F2.wireOp",EDGE,"E39.18.0.1");
            var Q24;
            Q24=sQuery(id+"F2.wireOp",EDGE,"E39.13.0.0");
            var Q25;
            Q25=sQuery(id+"F2.wireOp",EDGE,"E39.10.0.1");
            var Q26;
            Q26=sQuery(id+"F2.wireOp",EDGE,"E39.2.0.0");
            var Q27;
            Q27=sQuery(id+"F2.wireOp",EDGE,"E39.3.0.0");
            var Q28;
            Q28=sQuery(id+"F2.wireOp",EDGE,"E39.4.0.0");
            var Q29;
            Q29=sQuery(id+"F2.wireOp",EDGE,"E39.16.0.0");
            var Q30;
            Q30=sQuery(id+"F2.wireOp",EDGE,"E39.5.0.1");
            var Q31;
            Q31=sQuery(id+"F2.wireOp",EDGE,"E39.11.0.1");
            var Q32;
            Q32=sQuery(id+"F2.wireOp",EDGE,"E38");
            var Q33;
            Q33=sQuery(id+"F2.wireOp",EDGE,"E39.9.0.0");
            var Q34;
            Q34=sQuery(id+"F2.wireOp",EDGE,"E39.7.0.1");
            var Q35;
            Q35=sQuery(id+"F2.wireOp",EDGE,"E39.16.0.1");
            var Q36;
            Q36=sQuery(id+"F2.wireOp",EDGE,"E39.6.0.1");
            var Q37;
            Q37=sQuery(id+"F2.wireOp",EDGE,"E39.2.0.1");
            var Q38;
            Q38=sQuery(id+"F2.wireOp",EDGE,"E39.13.0.1");
            var Q39;
            Q39=sQuery(id+"F2.wireOp",EDGE,"E39.10.0.0");
            var Q40;
            Q40=sQuery(id+"F2.wireOp",EDGE,"E39.3.0.1");
            var Q41;
            Q41=sQuery(id+"F2.wireOp",EDGE,"E39.1.0.0");
            var Q42;
            Q42=sQuery(id+"F2.wireOp",EDGE,"E39.17.0.1");
            var Q43;
            Q43=sQuery(id+"F2.wireOp",EDGE,"E39.5.0.0");
            var Q44;
            Q44=sQuery(id+"F2.wireOp",EDGE,"E39.8.0.0");
            var Q45;
            Q45=sQuery(id+"F2.wireOp",EDGE,"E39.1.0.1");
            var Q46;
            Q46=sQuery(id+"F2.wireOp",EDGE,"E39.12.0.1");
            var Q47;
            Q47=sQuery(id+"F2.wireOp",EDGE,"E39.19.0.0");
            var Q48;
            Q48=sQuery(id+"F2.wireOp",EDGE,"E39.9.0.1");
            var Q49;
            Q49=sQuery(id+"F2.wireOp",EDGE,"E39.12.0.0");
            var Q50;
            Q50=sQuery(id+"F2.wireOp",EDGE,"E39.17.0.0");
            var Q51;
            Q51=sQuery(id+"F2.wireOp",EDGE,"E39.14.0.0");
            var Q52;
            Q52=sQuery(id+"F2.wireOp",EDGE,"E39.19.0.1");
            var Q53;
            Q53=sQuery(id+"F2.wireOp",EDGE,"E39.7.0.0");
            var Q54;
            Q54=sQuery(id+"F2.wireOp",EDGE,"E39.4.0.1");
            var Q55;
            Q55=sQuery(id+"F2.wireOp",EDGE,"E39.6.0.0");
            var Q56;
            Q56=sQuery(id+"F2.wireOp",EDGE,"E39.14.0.1");
            var Q57;
            Q57=sQuery(id+"F2.wireOp",EDGE,"E39.15.0.0");
            var Q58;
            Q58=sQuery(id+"F2.wireOp",EDGE,"E39.15.0.1");
            var Q59;
            Q59=sQuery(id+"F2.wireOp",EDGE,"E39.8.0.1");
            var Q60;
            Q60=sQuery(id+"F2.wireOp",EDGE,"E39.18.0.0");
            var Q61;
            Q61=sQuery(id+"F2.wireOp",EDGE,"E39.10.0.2");
            var Q62;
            Q62=sQuery(id+"F2.wireOp",EDGE,"E39.8.0.2");
            var Q63;
            Q63=sQuery(id+"F2.wireOp",EDGE,"E39.11.0.2");
            var Q64;
            Q64=sQuery(id+"F2.wireOp",EDGE,"E39.6.0.2");
            var Q65;
            Q65=sQuery(id+"F2.wireOp",EDGE,"E39.9.0.2");
            var Q66;
            Q66=sQuery(id+"F2.wireOp",EDGE,"E39.15.0.2");
            var Q67;
            Q67=sQuery(id+"F2.wireOp",EDGE,"E39.17.0.2");
            var Q68;
            Q68=sQuery(id+"F2.wireOp",EDGE,"E39.7.0.2");
            var Q69;
            Q69=sQuery(id+"F2.wireOp",EDGE,"E39.3.0.2");
            var Q70;
            Q70=sQuery(id+"F2.wireOp",EDGE,"E39.19.0.2");
            var Q71;
            Q71=sQuery(id+"F2.wireOp",EDGE,"E39.2.0.2");
            var Q72;
            Q72=sQuery(id+"F2.wireOp",EDGE,"E39.18.0.2");
            var Q73;
            Q73=sQuery(id+"F2.wireOp",EDGE,"E39.14.0.2");
            var Q74;
            Q74=sQuery(id+"F2.wireOp",EDGE,"E39.4.0.2");
            var Q75;
            Q75=sQuery(id+"F2.wireOp",EDGE,"E39.12.0.2");
            var Q76;
            Q76=sQuery(id+"F2.wireOp",EDGE,"E39.13.0.2");
            var Q77;
            Q77=sQuery(id+"F2.wireOp",EDGE,"E39.5.0.2");
            var Q78;
            Q78=sQuery(id+"F2.wireOp",EDGE,"E39.16.0.2");
            var Q79;
            Q79=sQuery(id+"F2.wireOp",EDGE,"E36");
            var Q80;
            Q80=sQuery(id+"F2.wireOp",EDGE,"E39.1.0.2");
            var Q81;
            Q81=sQuery(id+"F2.wireOp",EDGE,"E37");
            extrude(context, id + "F5", {"entities" : qUnion([Q0, Q1, Q2, Q3, Q4, Q5, Q6, Q7, Q8, Q9, Q10, Q11, Q12, Q13, Q14, Q15, Q16, Q17, Q18, Q19, Q20, Q21]), "operationType" : NewBodyOperationType.ADD, "surfaceEntities" : qUnion([Q22, Q23, Q24, Q25, Q26, Q27, Q28, Q29, Q30, Q31, Q32, Q33, Q34, Q35, Q36, Q37, Q38, Q39, Q40, Q41, Q42, Q43, Q44, Q45, Q46, Q47, Q48, Q49, Q50, Q51, Q52, Q53, Q54, Q55, Q56, Q57, Q58, Q59, Q60, Q61, Q62, Q63, Q64, Q65, Q66, Q67, Q68, Q69, Q70, Q71, Q72, Q73, Q74, Q75, Q76, Q77, Q78, Q79, Q80, Q81]), "depth" : 4 * mm, "offsetDistance" : 25 * mm});
        }
        {
            var Q0;
            Q0=makeQuery(id+"FGCFKRdd1TY3BEo_3.boolean.opBoolean","COPY",EDGE,{"derivedFrom":makeQuery(id+"FGCFKRdd1TY3BEo_3.opExtrude","SWEPT_EDGE",EDGE,{"disambiguationData":[OSD([sQuery(id+"F0.wireOp",EDGE,"E15.0"),sQuery(id+"F0.wireOp",EDGE,"E16.2")])]})});
            var Q1;
            Q1=makeQuery(id+"FGCFKRdd1TY3BEo_3.boolean.opBoolean","COPY",EDGE,{"derivedFrom":makeQuery(id+"FGCFKRdd1TY3BEo_3.opExtrude","SWEPT_EDGE",EDGE,{"disambiguationData":[OSD([sQuery(id+"F0.wireOp",EDGE,"E16.1"),sQuery(id+"F0.wireOp",EDGE,"E16.2")])]})});
            var Q2;
            Q2=makeQuery(id+"FGCFKRdd1TY3BEo_3.boolean.opBoolean","COPY",EDGE,{"derivedFrom":makeQuery(id+"FGCFKRdd1TY3BEo_3.opExtrude","SWEPT_EDGE",EDGE,{"disambiguationData":[OSD([sQuery(id+"F0.wireOp",EDGE,"7c9a6aae-f412-4e27-b171-df1cd759398a.0"),sQuery(id+"F0.wireOp",EDGE,"E16.1")])]})});
            var Q3;
            Q3=makeQuery(id+"FGCFKRdd1TY3BEo_3.boolean.opBoolean","COPY",EDGE,{"derivedFrom":makeQuery(id+"FGCFKRdd1TY3BEo_3.opExtrude","SWEPT_EDGE",EDGE,{"disambiguationData":[OSD([sQuery(id+"F0.wireOp",EDGE,"E13.0"),sQuery(id+"F0.wireOp",EDGE,"E16.1")])]})});
            var Q4;
            Q4=makeQuery(id+"FGCFKRdd1TY3BEo_3.boolean.opBoolean","COPY",EDGE,{"derivedFrom":makeQuery(id+"FGCFKRdd1TY3BEo_3.opExtrude","SWEPT_EDGE",EDGE,{"disambiguationData":[OSD([sQuery(id+"F0.wireOp",EDGE,"E16.0"),sQuery(id+"F0.wireOp",EDGE,"E16.1")])]})});
            var Q5;
            Q5=makeQuery(id+"FGCFKRdd1TY3BEo_3.boolean.opBoolean","COPY",EDGE,{"derivedFrom":makeQuery(id+"FGCFKRdd1TY3BEo_3.opExtrude","SWEPT_EDGE",EDGE,{"disambiguationData":[OSD([sQuery(id+"F0.wireOp",EDGE,"E16.0"),sQuery(id+"F0.wireOp",EDGE,"E16.2")])]})});
            var Q6;
            Q6=makeQuery(id+"FGCFKRdd1TY3BEo_3.boolean.opBoolean","COPY",EDGE,{"derivedFrom":makeQuery(id+"FGCFKRdd1TY3BEo_3.opExtrude","SWEPT_EDGE",EDGE,{"disambiguationData":[OSD([sQuery(id+"F0.wireOp",EDGE,"E14.0"),sQuery(id+"F0.wireOp",EDGE,"E16.2")])]})});
            var Q7;
            Q7=makeQuery(id+"FGCFKRdd1TY3BEo_3.boolean.opBoolean","COPY",EDGE,{"derivedFrom":makeQuery(id+"FGCFKRdd1TY3BEo_3.opExtrude","SWEPT_EDGE",EDGE,{"disambiguationData":[OSD([sQuery(id+"F0.wireOp",EDGE,"E11.0"),sQuery(id+"F0.wireOp",EDGE,"E16.0")])]})});
            var Q8;
            Q8=makeQuery(id+"FGCFKRdd1TY3BEo_3.boolean.opBoolean","COPY",EDGE,{"derivedFrom":makeQuery(id+"FGCFKRdd1TY3BEo_3.opExtrude","SWEPT_EDGE",EDGE,{"disambiguationData":[OSD([sQuery(id+"F0.wireOp",EDGE,"E12.0"),sQuery(id+"F0.wireOp",EDGE,"E16.0")])]})});
            var Q9;
            Q9=makeQuery(id+"F1.opExtrude","SWEPT_EDGE",EDGE,{"disambiguationData":[OSD([sQuery(id+"F0.wireOp",EDGE,"E0.0"),sQuery(id+"F0.wireOp",EDGE,"E0.1")])]});
            var Q10;
            Q10=makeQuery(id+"F1.opExtrude","SWEPT_EDGE",EDGE,{"disambiguationData":[OSD([sQuery(id+"F0.wireOp",EDGE,"E0.0"),sQuery(id+"F0.wireOp",EDGE,"E0.2")])]});
            var Q11;
            Q11=makeQuery(id+"F1.opExtrude","SWEPT_EDGE",EDGE,{"disambiguationData":[OSD([sQuery(id+"F0.wireOp",EDGE,"E0.1"),sQuery(id+"F0.wireOp",EDGE,"E0.2")])]});
            fillet(context, id + "F6", {"entities" : qUnion([Q0, Q1, Q2, Q3, Q4, Q5, Q6, Q7, Q8, Q9, Q10, Q11]), "radius" : 5 * mm, "tangentPropagation" : true, "allowEdgeOverflow" : false});
        }
        {
            var Q0;
            Q0=qCreatedBy(makeId("Top.planeOp"),FACE);
            var sketch = newSketch(context, id + "F7", { "sketchPlane" : qUnion([Q0])});
            skCircle(sketch, "E41", {"center": v(0, 0) * mm, "radius": 38 * mm});
            skCircle(sketch, "E42.0", {"center": v(0, 0) * mm, "radius": 33 * mm});
            skLineSegment(sketch, "E43.bottom", {"start": v(2.5, -32.9) * mm, "end": v(-2.5, -32.9) * mm});
            skLineSegment(sketch, "E43.top", {"start": v(2.5, 32.9) * mm, "end": v(-2.5, 32.9) * mm});
            skLineSegment(sketch, "E44.left", {"start": v(32.9, -2.5) * mm, "end": v(32.9, 2.5) * mm});
            skLineSegment(sketch, "E44.right", {"start": v(-32.9, -2.5) * mm, "end": v(-32.9, 2.5) * mm});
            skCircle(sketch, "E45.0", {"center": v(0, 0) * mm, "radius": 42 * mm, "construction": true});
            skLineSegment(sketch, "E46", {"start": v(0, 38) * mm, "end": v(0.86, 42) * mm});
            skLineSegment(sketch, "E47", {"start": v(0.86, 42) * mm, "end": v(2.36, 41.93) * mm});
            skLineSegment(sketch, "E48", {"start": v(2.36, 41.93) * mm, "end": v(2.92, 37.89) * mm});
            skLineSegment(sketch, "E49.1.0", {"start": v(-4.57, 41.75) * mm, "end": v(-3.36, 37.85) * mm});
            skLineSegment(sketch, "E49.1.1", {"start": v(-6.25, 37.48) * mm, "end": v(-6.06, 41.56) * mm});
            skLineSegment(sketch, "E49.1.2", {"start": v(-6.06, 41.56) * mm, "end": v(-4.57, 41.75) * mm});
            skLineSegment(sketch, "E49.2.0", {"start": v(-11.38, 40.43) * mm, "end": v(-9.54, 36.78) * mm});
            skLineSegment(sketch, "E49.2.1", {"start": v(-12.34, 35.94) * mm, "end": v(-12.82, 40) * mm});
            skLineSegment(sketch, "E49.2.2", {"start": v(-12.82, 40) * mm, "end": v(-11.38, 40.43) * mm});
            skLineSegment(sketch, "E49.3.0", {"start": v(-17.88, 38) * mm, "end": v(-15.47, 34.7) * mm});
            skLineSegment(sketch, "E49.3.1", {"start": v(-18.09, 33.42) * mm, "end": v(-19.23, 37.34) * mm});
            skLineSegment(sketch, "E49.3.2", {"start": v(-19.23, 37.34) * mm, "end": v(-17.88, 38) * mm});
            skLineSegment(sketch, "E49.4.0", {"start": v(-23.9, 34.54) * mm, "end": v(-20.97, 31.69) * mm});
            skLineSegment(sketch, "E49.4.1", {"start": v(-23.34, 29.99) * mm, "end": v(-25.11, 33.67) * mm});
            skLineSegment(sketch, "E49.4.2", {"start": v(-25.11, 33.67) * mm, "end": v(-23.9, 34.54) * mm});
            skLineSegment(sketch, "E49.5.0", {"start": v(-29.25, 30.14) * mm, "end": v(-25.9, 27.8) * mm});
            skLineSegment(sketch, "E49.5.1", {"start": v(-27.96, 25.74) * mm, "end": v(-30.3, 29.07) * mm});
            skLineSegment(sketch, "E49.5.2", {"start": v(-30.3, 29.07) * mm, "end": v(-29.25, 30.14) * mm});
            skLineSegment(sketch, "E49.6.0", {"start": v(-33.81, 24.91) * mm, "end": v(-30.12, 23.16) * mm});
            skLineSegment(sketch, "E49.6.1", {"start": v(-31.81, 20.78) * mm, "end": v(-34.68, 23.69) * mm});
            skLineSegment(sketch, "E49.6.2", {"start": v(-34.68, 23.69) * mm, "end": v(-33.81, 24.91) * mm});
            skLineSegment(sketch, "E49.7.0", {"start": v(-37.45, 19) * mm, "end": v(-33.53, 17.89) * mm});
            skLineSegment(sketch, "E49.7.1", {"start": v(-34.8, 15.26) * mm, "end": v(-38.1, 17.66) * mm});
            skLineSegment(sketch, "E49.7.2", {"start": v(-38.1, 17.66) * mm, "end": v(-37.45, 19) * mm});
            skLineSegment(sketch, "E49.8.0", {"start": v(-40.07, 12.58) * mm, "end": v(-36.01, 12.13) * mm});
            skLineSegment(sketch, "E49.8.1", {"start": v(-36.84, 9.33) * mm, "end": v(-40.5, 11.14) * mm});
            skLineSegment(sketch, "E49.8.2", {"start": v(-40.5, 11.14) * mm, "end": v(-40.07, 12.58) * mm});
            skLineSegment(sketch, "E49.9.0", {"start": v(-41.6, 5.82) * mm, "end": v(-37.52, 6.03) * mm});
            skLineSegment(sketch, "E49.9.1", {"start": v(-37.87, 3.14) * mm, "end": v(-41.78, 4.33) * mm});
            skLineSegment(sketch, "E49.9.2", {"start": v(-41.78, 4.33) * mm, "end": v(-41.6, 5.82) * mm});
            skLineSegment(sketch, "E49.10.0", {"start": v(-41.99, -1.1) * mm, "end": v(-38, -0.22) * mm});
            skLineSegment(sketch, "E49.10.1", {"start": v(-37.87, -3.14) * mm, "end": v(-41.92, -2.6) * mm});
            skLineSegment(sketch, "E49.10.2", {"start": v(-41.92, -2.6) * mm, "end": v(-41.99, -1.1) * mm});
            skLineSegment(sketch, "E49.11.0", {"start": v(-41.23, -8) * mm, "end": v(-37.44, -6.47) * mm});
            skLineSegment(sketch, "E49.11.1", {"start": v(-36.84, -9.33) * mm, "end": v(-40.92, -9.47) * mm});
            skLineSegment(sketch, "E49.11.2", {"start": v(-40.92, -9.47) * mm, "end": v(-41.23, -8) * mm});
            skLineSegment(sketch, "E49.12.0", {"start": v(-39.35, -14.68) * mm, "end": v(-35.87, -12.55) * mm});
            skLineSegment(sketch, "E49.12.1", {"start": v(-34.8, -15.26) * mm, "end": v(-38.8, -16.08) * mm});
            skLineSegment(sketch, "E49.12.2", {"start": v(-38.8, -16.08) * mm, "end": v(-39.35, -14.68) * mm});
            skLineSegment(sketch, "E49.13.0", {"start": v(-36.4, -20.96) * mm, "end": v(-33.31, -18.28) * mm});
            skLineSegment(sketch, "E49.13.1", {"start": v(-31.81, -20.78) * mm, "end": v(-35.63, -22.24) * mm});
            skLineSegment(sketch, "E49.13.2", {"start": v(-35.63, -22.24) * mm, "end": v(-36.4, -20.96) * mm});
            skLineSegment(sketch, "E49.14.0", {"start": v(-32.45, -26.66) * mm, "end": v(-29.85, -23.52) * mm});
            skLineSegment(sketch, "E49.14.1", {"start": v(-27.96, -25.74) * mm, "end": v(-31.48, -27.8) * mm});
            skLineSegment(sketch, "E49.14.2", {"start": v(-31.48, -27.8) * mm, "end": v(-32.45, -26.66) * mm});
            skLineSegment(sketch, "E49.15.0", {"start": v(-27.62, -31.64) * mm, "end": v(-25.57, -28.1) * mm});
            skLineSegment(sketch, "E49.15.1", {"start": v(-23.34, -29.99) * mm, "end": v(-26.47, -32.6) * mm});
            skLineSegment(sketch, "E49.15.2", {"start": v(-26.47, -32.6) * mm, "end": v(-27.62, -31.64) * mm});
            skLineSegment(sketch, "E49.16.0", {"start": v(-22.04, -35.76) * mm, "end": v(-20.6, -31.93) * mm});
            skLineSegment(sketch, "E49.16.1", {"start": v(-18.09, -33.42) * mm, "end": v(-20.74, -36.52) * mm});
            skLineSegment(sketch, "E49.16.2", {"start": v(-20.74, -36.52) * mm, "end": v(-22.04, -35.76) * mm});
            skLineSegment(sketch, "E49.17.0", {"start": v(-15.85, -38.9) * mm, "end": v(-15.06, -34.89) * mm});
            skLineSegment(sketch, "E49.17.1", {"start": v(-12.34, -35.94) * mm, "end": v(-14.45, -39.44) * mm});
            skLineSegment(sketch, "E49.17.2", {"start": v(-14.45, -39.44) * mm, "end": v(-15.85, -38.9) * mm});
            skLineSegment(sketch, "E50.3.18.0", {"start": v(-6.25, -37.48) * mm, "end": v(-7.76, -41.28) * mm});
            skLineSegment(sketch, "E50.4.18.0", {"start": v(-9.23, -40.97) * mm, "end": v(-9.11, -36.9) * mm});
            skLineSegment(sketch, "E50.6.18.0", {"start": v(-7.76, -41.28) * mm, "end": v(-9.23, -40.97) * mm});
            skLineSegment(sketch, "E50.3.19.0", {"start": v(0, -38) * mm, "end": v(-0.86, -42) * mm});
            skLineSegment(sketch, "E50.4.19.0", {"start": v(-2.36, -41.93) * mm, "end": v(-2.92, -37.89) * mm});
            skLineSegment(sketch, "E50.6.19.0", {"start": v(-0.86, -42) * mm, "end": v(-2.36, -41.93) * mm});
            skLineSegment(sketch, "E50.3.20.0", {"start": v(6.25, -37.48) * mm, "end": v(6.06, -41.56) * mm});
            skLineSegment(sketch, "E50.4.20.0", {"start": v(4.57, -41.75) * mm, "end": v(3.36, -37.85) * mm});
            skLineSegment(sketch, "E50.6.20.0", {"start": v(6.06, -41.56) * mm, "end": v(4.57, -41.75) * mm});
            skLineSegment(sketch, "E50.3.21.0", {"start": v(12.34, -35.94) * mm, "end": v(12.82, -40) * mm});
            skLineSegment(sketch, "E50.4.21.0", {"start": v(11.38, -40.43) * mm, "end": v(9.54, -36.78) * mm});
            skLineSegment(sketch, "E50.6.21.0", {"start": v(12.82, -40) * mm, "end": v(11.38, -40.43) * mm});
            skLineSegment(sketch, "E50.3.22.0", {"start": v(18.09, -33.42) * mm, "end": v(19.23, -37.34) * mm});
            skLineSegment(sketch, "E50.4.22.0", {"start": v(17.88, -38) * mm, "end": v(15.47, -34.7) * mm});
            skLineSegment(sketch, "E50.6.22.0", {"start": v(19.23, -37.34) * mm, "end": v(17.88, -38) * mm});
            skLineSegment(sketch, "E50.3.23.0", {"start": v(23.34, -29.99) * mm, "end": v(25.11, -33.67) * mm});
            skLineSegment(sketch, "E50.4.23.0", {"start": v(23.9, -34.54) * mm, "end": v(20.97, -31.69) * mm});
            skLineSegment(sketch, "E50.6.23.0", {"start": v(25.11, -33.67) * mm, "end": v(23.9, -34.54) * mm});
            skLineSegment(sketch, "E50.3.24.0", {"start": v(27.96, -25.74) * mm, "end": v(30.3, -29.07) * mm});
            skLineSegment(sketch, "E50.4.24.0", {"start": v(29.25, -30.14) * mm, "end": v(25.9, -27.8) * mm});
            skLineSegment(sketch, "E50.6.24.0", {"start": v(30.3, -29.07) * mm, "end": v(29.25, -30.14) * mm});
            skLineSegment(sketch, "E50.3.25.0", {"start": v(31.81, -20.78) * mm, "end": v(34.68, -23.69) * mm});
            skLineSegment(sketch, "E50.4.25.0", {"start": v(33.81, -24.91) * mm, "end": v(30.12, -23.16) * mm});
            skLineSegment(sketch, "E50.6.25.0", {"start": v(34.68, -23.69) * mm, "end": v(33.81, -24.91) * mm});
            skLineSegment(sketch, "E50.3.26.0", {"start": v(34.8, -15.26) * mm, "end": v(38.1, -17.66) * mm});
            skLineSegment(sketch, "E50.4.26.0", {"start": v(37.45, -19) * mm, "end": v(33.53, -17.89) * mm});
            skLineSegment(sketch, "E50.6.26.0", {"start": v(38.1, -17.66) * mm, "end": v(37.45, -19) * mm});
            skLineSegment(sketch, "E50.3.27.0", {"start": v(36.84, -9.33) * mm, "end": v(40.5, -11.14) * mm});
            skLineSegment(sketch, "E50.4.27.0", {"start": v(40.07, -12.58) * mm, "end": v(36.01, -12.13) * mm});
            skLineSegment(sketch, "E50.6.27.0", {"start": v(40.5, -11.14) * mm, "end": v(40.07, -12.58) * mm});
            skLineSegment(sketch, "E50.3.28.0", {"start": v(37.87, -3.14) * mm, "end": v(41.78, -4.33) * mm});
            skLineSegment(sketch, "E50.4.28.0", {"start": v(41.6, -5.82) * mm, "end": v(37.52, -6.03) * mm});
            skLineSegment(sketch, "E50.6.28.0", {"start": v(41.78, -4.33) * mm, "end": v(41.6, -5.82) * mm});
            skLineSegment(sketch, "E50.3.29.0", {"start": v(37.87, 3.14) * mm, "end": v(41.92, 2.6) * mm});
            skLineSegment(sketch, "E50.4.29.0", {"start": v(41.99, 1.1) * mm, "end": v(38, 0.22) * mm});
            skLineSegment(sketch, "E50.6.29.0", {"start": v(41.92, 2.6) * mm, "end": v(41.99, 1.1) * mm});
            skLineSegment(sketch, "E50.3.30.0", {"start": v(36.84, 9.33) * mm, "end": v(40.92, 9.47) * mm});
            skLineSegment(sketch, "E50.4.30.0", {"start": v(41.23, 8) * mm, "end": v(37.44, 6.47) * mm});
            skLineSegment(sketch, "E50.6.30.0", {"start": v(40.92, 9.47) * mm, "end": v(41.23, 8) * mm});
            skLineSegment(sketch, "E50.3.31.0", {"start": v(34.8, 15.26) * mm, "end": v(38.8, 16.08) * mm});
            skLineSegment(sketch, "E50.4.31.0", {"start": v(39.35, 14.68) * mm, "end": v(35.87, 12.55) * mm});
            skLineSegment(sketch, "E50.6.31.0", {"start": v(38.8, 16.08) * mm, "end": v(39.35, 14.68) * mm});
            skLineSegment(sketch, "E50.3.32.0", {"start": v(31.81, 20.78) * mm, "end": v(35.63, 22.24) * mm});
            skLineSegment(sketch, "E50.4.32.0", {"start": v(36.4, 20.96) * mm, "end": v(33.31, 18.28) * mm});
            skLineSegment(sketch, "E50.6.32.0", {"start": v(35.63, 22.24) * mm, "end": v(36.4, 20.96) * mm});
            skLineSegment(sketch, "E50.3.33.0", {"start": v(27.96, 25.74) * mm, "end": v(31.48, 27.8) * mm});
            skLineSegment(sketch, "E50.4.33.0", {"start": v(32.45, 26.66) * mm, "end": v(29.85, 23.52) * mm});
            skLineSegment(sketch, "E50.6.33.0", {"start": v(31.48, 27.8) * mm, "end": v(32.45, 26.66) * mm});
            skLineSegment(sketch, "E50.3.34.0", {"start": v(23.34, 29.99) * mm, "end": v(26.47, 32.6) * mm});
            skLineSegment(sketch, "E50.4.34.0", {"start": v(27.62, 31.64) * mm, "end": v(25.57, 28.1) * mm});
            skLineSegment(sketch, "E50.6.34.0", {"start": v(26.47, 32.6) * mm, "end": v(27.62, 31.64) * mm});
            skLineSegment(sketch, "E50.3.35.0", {"start": v(18.09, 33.42) * mm, "end": v(20.74, 36.52) * mm});
            skLineSegment(sketch, "E50.4.35.0", {"start": v(22.04, 35.76) * mm, "end": v(20.6, 31.93) * mm});
            skLineSegment(sketch, "E50.6.35.0", {"start": v(20.74, 36.52) * mm, "end": v(22.04, 35.76) * mm});
            skLineSegment(sketch, "E50.3.36.0", {"start": v(12.34, 35.94) * mm, "end": v(14.45, 39.44) * mm});
            skLineSegment(sketch, "E50.4.36.0", {"start": v(15.85, 38.9) * mm, "end": v(15.06, 34.89) * mm});
            skLineSegment(sketch, "E50.6.36.0", {"start": v(14.45, 39.44) * mm, "end": v(15.85, 38.9) * mm});
            skLineSegment(sketch, "E50.3.37.0", {"start": v(6.25, 37.48) * mm, "end": v(7.76, 41.28) * mm});
            skLineSegment(sketch, "E50.4.37.0", {"start": v(9.23, 40.97) * mm, "end": v(9.11, 36.9) * mm});
            skLineSegment(sketch, "E50.6.37.0", {"start": v(7.76, 41.28) * mm, "end": v(9.23, 40.97) * mm});
            skCircle(sketch, "E51", {"center": v(0, 0) * mm, "radius": 3.25 * mm});
            skLineSegment(sketch, "E52", {"start": v(-2.4, 2.2) * mm, "end": v(-2.4, -2.2) * mm});
            skCircle(sketch, "E53.0", {"center": v(0, 0) * mm, "radius": 8.25 * mm});
            skLineSegment(sketch, "E54", {"start": v(-2.5, -32.9) * mm, "end": v(-2.5, -7.86) * mm});
            skLineSegment(sketch, "E55", {"start": v(2.5, -32.9) * mm, "end": v(2.5, -7.86) * mm});
            skLineSegment(sketch, "E56", {"start": v(0, 0) * mm, "end": v(-28.58, 16.5) * mm, "construction": true});
            skLineSegment(sketch, "E57", {"start": v(0, 0) * mm, "end": v(28.58, 16.5) * mm, "construction": true});
            skLineSegment(sketch, "E58.0", {"start": v(1.25, 2.17) * mm, "end": v(-27.33, 18.67) * mm});
            skLineSegment(sketch, "E59.0", {"start": v(-1.25, -2.17) * mm, "end": v(-29.83, 14.33) * mm});
            skLineSegment(sketch, "E60.0", {"start": v(1.25, -2.17) * mm, "end": v(29.83, 14.33) * mm});
            skLineSegment(sketch, "E61.0", {"start": v(-1.25, 2.17) * mm, "end": v(27.33, 18.67) * mm});
            skSolve(sketch);
        }
        {
            var Q0;
            Q0=makeQuery(id+"F7.imprint","IMPRINT",FACE,{"disambiguationData":[TD([[makeQuery(id+"F7.imprint","IMPRINT",EDGE,{"derivedFrom":sQuery(id+"F7.wireOp",EDGE,"E43.bottom")}),-1.0]])]});
            var Q1;
            {var subQ0=sQuery(id+"F7.wireOp",EDGE,"E41");var subQ33=makeQuery(id+"F7.imprint","INTERSECT",VERTEX,{"derivedFrom":[subQ0,sQuery(id+"F7.wireOp",EDGE,"E50.3.29.0")]});Q1=makeQuery(id+"F7.imprint","IMPRINT",FACE,{"disambiguationData":[TD([[makeQuery(id+"F7.imprint","IMPRINT",EDGE,{"disambiguationData":[TD([[subQ33,1.0]])],"derivedFrom":subQ0}),1.0]])]});}
            var Q2;
            {var subQ0=sQuery(id+"F7.wireOp",EDGE,"E49.16.0");Q2=makeQuery(id+"F7.imprint","IMPRINT",FACE,{"disambiguationData":[TD([[makeQuery(id+"F7.imprint","IMPRINT",EDGE,{"derivedFrom":subQ0}),-1.0]])]});}
            var Q3;
            {var subQ0=sQuery(id+"F7.wireOp",EDGE,"E50.3.36.0");Q3=makeQuery(id+"F7.imprint","IMPRINT",FACE,{"disambiguationData":[TD([[makeQuery(id+"F7.imprint","IMPRINT",EDGE,{"derivedFrom":subQ0}),-1.0]])]});}
            var Q4;
            {var subQ0=sQuery(id+"F7.wireOp",EDGE,"E49.2.0");Q4=makeQuery(id+"F7.imprint","IMPRINT",FACE,{"disambiguationData":[TD([[makeQuery(id+"F7.imprint","IMPRINT",EDGE,{"derivedFrom":subQ0}),-1.0]])]});}
            var Q5;
            {var subQ0=sQuery(id+"F7.wireOp",EDGE,"E49.6.0");Q5=makeQuery(id+"F7.imprint","IMPRINT",FACE,{"disambiguationData":[TD([[makeQuery(id+"F7.imprint","IMPRINT",EDGE,{"derivedFrom":subQ0}),-1.0]])]});}
            var Q6;
            {var subQ0=sQuery(id+"F7.wireOp",EDGE,"E50.3.30.0");Q6=makeQuery(id+"F7.imprint","IMPRINT",FACE,{"disambiguationData":[TD([[makeQuery(id+"F7.imprint","IMPRINT",EDGE,{"derivedFrom":subQ0}),-1.0]])]});}
            var Q7;
            {var subQ0=sQuery(id+"F7.wireOp",EDGE,"E49.17.0");Q7=makeQuery(id+"F7.imprint","IMPRINT",FACE,{"disambiguationData":[TD([[makeQuery(id+"F7.imprint","IMPRINT",EDGE,{"derivedFrom":subQ0}),-1.0]])]});}
            var Q8;
            {var subQ0=sQuery(id+"F7.wireOp",EDGE,"E50.3.37.0");Q8=makeQuery(id+"F7.imprint","IMPRINT",FACE,{"disambiguationData":[TD([[makeQuery(id+"F7.imprint","IMPRINT",EDGE,{"derivedFrom":subQ0}),-1.0]])]});}
            var Q9;
            {var subQ0=sQuery(id+"F7.wireOp",EDGE,"E50.3.27.0");Q9=makeQuery(id+"F7.imprint","IMPRINT",FACE,{"disambiguationData":[TD([[makeQuery(id+"F7.imprint","IMPRINT",EDGE,{"derivedFrom":subQ0}),-1.0]])]});}
            var Q10;
            {var subQ0=sQuery(id+"F7.wireOp",EDGE,"E50.3.28.0");Q10=makeQuery(id+"F7.imprint","IMPRINT",FACE,{"disambiguationData":[TD([[makeQuery(id+"F7.imprint","IMPRINT",EDGE,{"derivedFrom":subQ0}),-1.0]])]});}
            var Q11;
            {var subQ0=sQuery(id+"F7.wireOp",EDGE,"E49.3.0");Q11=makeQuery(id+"F7.imprint","IMPRINT",FACE,{"disambiguationData":[TD([[makeQuery(id+"F7.imprint","IMPRINT",EDGE,{"derivedFrom":subQ0}),-1.0]])]});}
            var Q12;
            {var subQ0=sQuery(id+"F7.wireOp",EDGE,"E50.3.31.0");Q12=makeQuery(id+"F7.imprint","IMPRINT",FACE,{"disambiguationData":[TD([[makeQuery(id+"F7.imprint","IMPRINT",EDGE,{"derivedFrom":subQ0}),-1.0]])]});}
            var Q13;
            {var subQ0=sQuery(id+"F7.wireOp",EDGE,"E49.10.0");Q13=makeQuery(id+"F7.imprint","IMPRINT",FACE,{"disambiguationData":[TD([[makeQuery(id+"F7.imprint","IMPRINT",EDGE,{"derivedFrom":subQ0}),-1.0]])]});}
            var Q14;
            {var subQ0=sQuery(id+"F7.wireOp",EDGE,"E50.3.19.0");Q14=makeQuery(id+"F7.imprint","IMPRINT",FACE,{"disambiguationData":[TD([[makeQuery(id+"F7.imprint","IMPRINT",EDGE,{"derivedFrom":subQ0}),-1.0]])]});}
            var Q15;
            {var subQ0=sQuery(id+"F7.wireOp",EDGE,"E44.right");Q15=makeQuery(id+"F7.imprint","IMPRINT",FACE,{"disambiguationData":[TD([[makeQuery(id+"F7.imprint","IMPRINT",EDGE,{"derivedFrom":subQ0}),1.0]])]});}
            var Q16;
            {var subQ0=sQuery(id+"F7.wireOp",EDGE,"E50.3.23.0");Q16=makeQuery(id+"F7.imprint","IMPRINT",FACE,{"disambiguationData":[TD([[makeQuery(id+"F7.imprint","IMPRINT",EDGE,{"derivedFrom":subQ0}),-1.0]])]});}
            var Q17;
            {var subQ0=sQuery(id+"F7.wireOp",EDGE,"E49.15.0");Q17=makeQuery(id+"F7.imprint","IMPRINT",FACE,{"disambiguationData":[TD([[makeQuery(id+"F7.imprint","IMPRINT",EDGE,{"derivedFrom":subQ0}),-1.0]])]});}
            var Q18;
            {var subQ0=sQuery(id+"F7.wireOp",EDGE,"E49.13.0");Q18=makeQuery(id+"F7.imprint","IMPRINT",FACE,{"disambiguationData":[TD([[makeQuery(id+"F7.imprint","IMPRINT",EDGE,{"derivedFrom":subQ0}),-1.0]])]});}
            var Q19;
            {var subQ0=sQuery(id+"F7.wireOp",EDGE,"E50.3.25.0");Q19=makeQuery(id+"F7.imprint","IMPRINT",FACE,{"disambiguationData":[TD([[makeQuery(id+"F7.imprint","IMPRINT",EDGE,{"derivedFrom":subQ0}),-1.0]])]});}
            var Q20;
            {var subQ0=sQuery(id+"F7.wireOp",EDGE,"E43.bottom");Q20=makeQuery(id+"F7.imprint","IMPRINT",FACE,{"disambiguationData":[TD([[makeQuery(id+"F7.imprint","IMPRINT",EDGE,{"derivedFrom":subQ0}),1.0]])]});}
            var Q21;
            {var subQ0=sQuery(id+"F7.wireOp",EDGE,"E49.4.0");Q21=makeQuery(id+"F7.imprint","IMPRINT",FACE,{"disambiguationData":[TD([[makeQuery(id+"F7.imprint","IMPRINT",EDGE,{"derivedFrom":subQ0}),-1.0]])]});}
            var Q22;
            {var subQ0=sQuery(id+"F7.wireOp",EDGE,"E50.3.29.0");Q22=makeQuery(id+"F7.imprint","IMPRINT",FACE,{"disambiguationData":[TD([[makeQuery(id+"F7.imprint","IMPRINT",EDGE,{"derivedFrom":subQ0}),-1.0]])]});}
            var Q23;
            {var subQ0=sQuery(id+"F7.wireOp",EDGE,"E50.3.32.0");Q23=makeQuery(id+"F7.imprint","IMPRINT",FACE,{"disambiguationData":[TD([[makeQuery(id+"F7.imprint","IMPRINT",EDGE,{"derivedFrom":subQ0}),-1.0]])]});}
            var Q24;
            {var subQ0=sQuery(id+"F7.wireOp",EDGE,"E44.left");Q24=makeQuery(id+"F7.imprint","IMPRINT",FACE,{"disambiguationData":[TD([[makeQuery(id+"F7.imprint","IMPRINT",EDGE,{"derivedFrom":subQ0}),-1.0]])]});}
            var Q25;
            {var subQ0=sQuery(id+"F7.wireOp",EDGE,"E49.12.0");Q25=makeQuery(id+"F7.imprint","IMPRINT",FACE,{"disambiguationData":[TD([[makeQuery(id+"F7.imprint","IMPRINT",EDGE,{"derivedFrom":subQ0}),-1.0]])]});}
            var Q26;
            {var subQ0=sQuery(id+"F7.wireOp",EDGE,"E43.top");Q26=makeQuery(id+"F7.imprint","IMPRINT",FACE,{"disambiguationData":[TD([[makeQuery(id+"F7.imprint","IMPRINT",EDGE,{"derivedFrom":subQ0}),-1.0]])]});}
            var Q27;
            {var subQ0=sQuery(id+"F7.wireOp",EDGE,"E49.1.0");Q27=makeQuery(id+"F7.imprint","IMPRINT",FACE,{"disambiguationData":[TD([[makeQuery(id+"F7.imprint","IMPRINT",EDGE,{"derivedFrom":subQ0}),-1.0]])]});}
            var Q28;
            {var subQ0=sQuery(id+"F7.wireOp",EDGE,"E49.8.0");Q28=makeQuery(id+"F7.imprint","IMPRINT",FACE,{"disambiguationData":[TD([[makeQuery(id+"F7.imprint","IMPRINT",EDGE,{"derivedFrom":subQ0}),-1.0]])]});}
            var Q29;
            {var subQ0=sQuery(id+"F7.wireOp",EDGE,"E50.3.21.0");Q29=makeQuery(id+"F7.imprint","IMPRINT",FACE,{"disambiguationData":[TD([[makeQuery(id+"F7.imprint","IMPRINT",EDGE,{"derivedFrom":subQ0}),-1.0]])]});}
            var Q30;
            {var subQ0=sQuery(id+"F7.wireOp",EDGE,"E49.11.0");Q30=makeQuery(id+"F7.imprint","IMPRINT",FACE,{"disambiguationData":[TD([[makeQuery(id+"F7.imprint","IMPRINT",EDGE,{"derivedFrom":subQ0}),-1.0]])]});}
            var Q31;
            {var subQ0=sQuery(id+"F7.wireOp",EDGE,"E49.5.0");Q31=makeQuery(id+"F7.imprint","IMPRINT",FACE,{"disambiguationData":[TD([[makeQuery(id+"F7.imprint","IMPRINT",EDGE,{"derivedFrom":subQ0}),-1.0]])]});}
            var Q32;
            {var subQ0=sQuery(id+"F7.wireOp",EDGE,"E50.3.26.0");Q32=makeQuery(id+"F7.imprint","IMPRINT",FACE,{"disambiguationData":[TD([[makeQuery(id+"F7.imprint","IMPRINT",EDGE,{"derivedFrom":subQ0}),-1.0]])]});}
            var Q33;
            {var subQ0=sQuery(id+"F7.wireOp",EDGE,"E50.3.20.0");Q33=makeQuery(id+"F7.imprint","IMPRINT",FACE,{"disambiguationData":[TD([[makeQuery(id+"F7.imprint","IMPRINT",EDGE,{"derivedFrom":subQ0}),-1.0]])]});}
            var Q34;
            {var subQ0=sQuery(id+"F7.wireOp",EDGE,"E49.7.0");Q34=makeQuery(id+"F7.imprint","IMPRINT",FACE,{"disambiguationData":[TD([[makeQuery(id+"F7.imprint","IMPRINT",EDGE,{"derivedFrom":subQ0}),-1.0]])]});}
            var Q35;
            {var subQ0=sQuery(id+"F7.wireOp",EDGE,"E46");Q35=makeQuery(id+"F7.imprint","IMPRINT",FACE,{"disambiguationData":[TD([[makeQuery(id+"F7.imprint","IMPRINT",EDGE,{"derivedFrom":subQ0}),-1.0]])]});}
            var Q36;
            {var subQ0=sQuery(id+"F7.wireOp",EDGE,"E50.3.33.0");Q36=makeQuery(id+"F7.imprint","IMPRINT",FACE,{"disambiguationData":[TD([[makeQuery(id+"F7.imprint","IMPRINT",EDGE,{"derivedFrom":subQ0}),-1.0]])]});}
            var Q37;
            {var subQ0=sQuery(id+"F7.wireOp",EDGE,"E49.9.0");Q37=makeQuery(id+"F7.imprint","IMPRINT",FACE,{"disambiguationData":[TD([[makeQuery(id+"F7.imprint","IMPRINT",EDGE,{"derivedFrom":subQ0}),-1.0]])]});}
            var Q38;
            {var subQ0=sQuery(id+"F7.wireOp",EDGE,"E50.3.34.0");Q38=makeQuery(id+"F7.imprint","IMPRINT",FACE,{"disambiguationData":[TD([[makeQuery(id+"F7.imprint","IMPRINT",EDGE,{"derivedFrom":subQ0}),-1.0]])]});}
            var Q39;
            {var subQ0=sQuery(id+"F7.wireOp",EDGE,"E50.3.35.0");Q39=makeQuery(id+"F7.imprint","IMPRINT",FACE,{"disambiguationData":[TD([[makeQuery(id+"F7.imprint","IMPRINT",EDGE,{"derivedFrom":subQ0}),-1.0]])]});}
            var Q40;
            {var subQ0=sQuery(id+"F7.wireOp",EDGE,"E49.14.0");Q40=makeQuery(id+"F7.imprint","IMPRINT",FACE,{"disambiguationData":[TD([[makeQuery(id+"F7.imprint","IMPRINT",EDGE,{"derivedFrom":subQ0}),-1.0]])]});}
            var Q41;
            {var subQ0=sQuery(id+"F7.wireOp",EDGE,"E50.3.22.0");Q41=makeQuery(id+"F7.imprint","IMPRINT",FACE,{"disambiguationData":[TD([[makeQuery(id+"F7.imprint","IMPRINT",EDGE,{"derivedFrom":subQ0}),-1.0]])]});}
            var Q42;
            {var subQ0=sQuery(id+"F7.wireOp",EDGE,"E50.3.24.0");Q42=makeQuery(id+"F7.imprint","IMPRINT",FACE,{"disambiguationData":[TD([[makeQuery(id+"F7.imprint","IMPRINT",EDGE,{"derivedFrom":subQ0}),-1.0]])]});}
            var Q43;
            {var subQ0=sQuery(id+"F7.wireOp",EDGE,"E50.3.18.0");Q43=makeQuery(id+"F7.imprint","IMPRINT",FACE,{"disambiguationData":[TD([[makeQuery(id+"F7.imprint","IMPRINT",EDGE,{"derivedFrom":subQ0}),-1.0]])]});}
            var Q44;
            {var subQ0=sQuery(id+"F7.wireOp",EDGE,"E58.0");var subQ1=sQuery(id+"F7.wireOp",EDGE,"E42.0");var subQ2=makeQuery(id+"F7.imprint","INTERSECT",VERTEX,{"derivedFrom":[subQ1,subQ0]});Q44=makeQuery(id+"F7.imprint","IMPRINT",FACE,{"disambiguationData":[TD([[makeQuery(id+"F7.imprint","IMPRINT",EDGE,{"disambiguationData":[TD([[subQ2,-1.0]])],"derivedFrom":subQ1}),1.0]])]});}
            var Q45;
            {var subQ0=sQuery(id+"F7.wireOp",EDGE,"E60.0");var subQ1=sQuery(id+"F7.wireOp",EDGE,"E42.0");var subQ2=makeQuery(id+"F7.imprint","INTERSECT",VERTEX,{"derivedFrom":[subQ1,subQ0]});Q45=makeQuery(id+"F7.imprint","IMPRINT",FACE,{"disambiguationData":[TD([[makeQuery(id+"F7.imprint","IMPRINT",EDGE,{"disambiguationData":[TD([[subQ2,-1.0]])],"derivedFrom":subQ1}),1.0]])]});}
            var Q46;
            {var subQ0=sQuery(id+"F7.wireOp",EDGE,"E61.0");var subQ1=sQuery(id+"F7.wireOp",EDGE,"E53.0");var subQ2=makeQuery(id+"F7.imprint","INTERSECT",VERTEX,{"derivedFrom":[subQ1,subQ0]});Q46=makeQuery(id+"F7.imprint","IMPRINT",FACE,{"disambiguationData":[TD([[makeQuery(id+"F7.imprint","IMPRINT",EDGE,{"disambiguationData":[TD([[subQ2,-1.0]])],"derivedFrom":subQ1}),1.0]])]});}
            var Q47;
            {var subQ5=sQuery(id+"F7.wireOp",EDGE,"E52");var subQ6=sQuery(id+"F7.wireOp",EDGE,"E51");var subQ9=makeQuery(id+"F7.imprint","INTERSECT",VERTEX,{"disambiguationData":[OD(0.0)],"derivedFrom":[subQ6,subQ5]});Q47=makeQuery(id+"F7.imprint","IMPRINT",FACE,{"disambiguationData":[TD([[makeQuery(id+"F7.imprint","IMPRINT",EDGE,{"disambiguationData":[TD([[subQ9,1.0]])],"derivedFrom":subQ6}),-1.0]])]});}
            var Q48;
            {var subQ5=sQuery(id+"F7.wireOp",EDGE,"E59.0");var subQ7=sQuery(id+"F7.wireOp",EDGE,"E51");var subQ8=makeQuery(id+"F7.imprint","INTERSECT",VERTEX,{"derivedFrom":[subQ7,subQ5]});Q48=makeQuery(id+"F7.imprint","IMPRINT",FACE,{"disambiguationData":[TD([[makeQuery(id+"F7.imprint","IMPRINT",EDGE,{"disambiguationData":[TD([[subQ8,-1.0]])],"derivedFrom":subQ7}),-1.0]])]});}
            var Q49;
            {var subQ5=sQuery(id+"F7.wireOp",EDGE,"E51");var subQ7=sQuery(id+"F7.wireOp",EDGE,"E58.0");var subQ8=makeQuery(id+"F7.imprint","INTERSECT",VERTEX,{"derivedFrom":[subQ5,subQ7]});Q49=makeQuery(id+"F7.imprint","IMPRINT",FACE,{"disambiguationData":[TD([[makeQuery(id+"F7.imprint","IMPRINT",EDGE,{"disambiguationData":[TD([[subQ8,1.0]])],"derivedFrom":subQ5}),-1.0]])]});}
            var Q50;
            {var subQ0=sQuery(id+"F7.wireOp",EDGE,"E60.0");var subQ1=sQuery(id+"F7.wireOp",EDGE,"E51");var subQ2=makeQuery(id+"F7.imprint","INTERSECT",VERTEX,{"derivedFrom":[subQ1,subQ0]});Q50=makeQuery(id+"F7.imprint","IMPRINT",FACE,{"disambiguationData":[TD([[makeQuery(id+"F7.imprint","IMPRINT",EDGE,{"disambiguationData":[TD([[subQ2,-1.0]])],"derivedFrom":subQ1}),-1.0]])]});}
            extrude(context, id + "F8", {"entities" : qUnion([Q0, Q1, Q2, Q3, Q4, Q5, Q6, Q7, Q8, Q9, Q10, Q11, Q12, Q13, Q14, Q15, Q16, Q17, Q18, Q19, Q20, Q21, Q22, Q23, Q24, Q25, Q26, Q27, Q28, Q29, Q30, Q31, Q32, Q33, Q34, Q35, Q36, Q37, Q38, Q39, Q40, Q41, Q42, Q43, Q44, Q45, Q46, Q47, Q48, Q49, Q50]), "depth" : 4 * mm, "offsetDistance" : 25 * mm});
        }
        {
            var Q0;
            Q0=makeQuery(id+"F8.opExtrude","CAP_FACE",FACE,{"disambiguationData":[OSD([sQuery(id+"F7.wireOp",EDGE,"E41"),sQuery(id+"F7.wireOp",EDGE,"E46"),sQuery(id+"F7.wireOp",EDGE,"E47"),sQuery(id+"F7.wireOp",EDGE,"E48"),sQuery(id+"F7.wireOp",EDGE,"E49.1.0"),sQuery(id+"F7.wireOp",EDGE,"E49.1.1"),sQuery(id+"F7.wireOp",EDGE,"E49.1.2"),sQuery(id+"F7.wireOp",EDGE,"E49.2.0"),sQuery(id+"F7.wireOp",EDGE,"E49.2.1"),sQuery(id+"F7.wireOp",EDGE,"E49.2.2"),sQuery(id+"F7.wireOp",EDGE,"E49.3.0"),sQuery(id+"F7.wireOp",EDGE,"E49.3.1"),sQuery(id+"F7.wireOp",EDGE,"E49.3.2"),sQuery(id+"F7.wireOp",EDGE,"E49.4.0"),sQuery(id+"F7.wireOp",EDGE,"E49.4.1"),sQuery(id+"F7.wireOp",EDGE,"E49.4.2"),sQuery(id+"F7.wireOp",EDGE,"E49.5.0"),sQuery(id+"F7.wireOp",EDGE,"E49.5.1"),sQuery(id+"F7.wireOp",EDGE,"E49.5.2"),sQuery(id+"F7.wireOp",EDGE,"E49.6.0"),sQuery(id+"F7.wireOp",EDGE,"E49.6.1"),sQuery(id+"F7.wireOp",EDGE,"E49.6.2"),sQuery(id+"F7.wireOp",EDGE,"E49.7.0"),sQuery(id+"F7.wireOp",EDGE,"E49.7.1"),sQuery(id+"F7.wireOp",EDGE,"E49.7.2"),sQuery(id+"F7.wireOp",EDGE,"E49.8.0"),sQuery(id+"F7.wireOp",EDGE,"E49.8.1"),sQuery(id+"F7.wireOp",EDGE,"E49.8.2"),sQuery(id+"F7.wireOp",EDGE,"E49.9.0"),sQuery(id+"F7.wireOp",EDGE,"E49.9.1"),sQuery(id+"F7.wireOp",EDGE,"E49.9.2"),sQuery(id+"F7.wireOp",EDGE,"E49.10.0"),sQuery(id+"F7.wireOp",EDGE,"E49.10.1"),sQuery(id+"F7.wireOp",EDGE,"E49.10.2"),sQuery(id+"F7.wireOp",EDGE,"E49.11.0"),sQuery(id+"F7.wireOp",EDGE,"E49.11.1"),sQuery(id+"F7.wireOp",EDGE,"E49.11.2"),sQuery(id+"F7.wireOp",EDGE,"E49.12.0"),sQuery(id+"F7.wireOp",EDGE,"E49.12.1"),sQuery(id+"F7.wireOp",EDGE,"E49.12.2"),sQuery(id+"F7.wireOp",EDGE,"E49.13.0"),sQuery(id+"F7.wireOp",EDGE,"E49.13.1"),sQuery(id+"F7.wireOp",EDGE,"E49.13.2"),sQuery(id+"F7.wireOp",EDGE,"E49.14.0"),sQuery(id+"F7.wireOp",EDGE,"E49.14.1"),sQuery(id+"F7.wireOp",EDGE,"E49.14.2"),sQuery(id+"F7.wireOp",EDGE,"E49.15.0"),sQuery(id+"F7.wireOp",EDGE,"E49.15.1"),sQuery(id+"F7.wireOp",EDGE,"E49.15.2"),sQuery(id+"F7.wireOp",EDGE,"E49.16.0"),sQuery(id+"F7.wireOp",EDGE,"E49.16.1"),sQuery(id+"F7.wireOp",EDGE,"E49.16.2"),sQuery(id+"F7.wireOp",EDGE,"E49.17.0"),sQuery(id+"F7.wireOp",EDGE,"E49.17.1"),sQuery(id+"F7.wireOp",EDGE,"E49.17.2"),sQuery(id+"F7.wireOp",EDGE,"E50.3.18.0"),sQuery(id+"F7.wireOp",EDGE,"E50.4.18.0"),sQuery(id+"F7.wireOp",EDGE,"E50.6.18.0"),sQuery(id+"F7.wireOp",EDGE,"E50.3.19.0"),sQuery(id+"F7.wireOp",EDGE,"E50.4.19.0"),sQuery(id+"F7.wireOp",EDGE,"E50.6.19.0"),sQuery(id+"F7.wireOp",EDGE,"E50.3.20.0"),sQuery(id+"F7.wireOp",EDGE,"E50.4.20.0"),sQuery(id+"F7.wireOp",EDGE,"E50.6.20.0"),sQuery(id+"F7.wireOp",EDGE,"E50.3.21.0"),sQuery(id+"F7.wireOp",EDGE,"E50.4.21.0"),sQuery(id+"F7.wireOp",EDGE,"E50.6.21.0"),sQuery(id+"F7.wireOp",EDGE,"E50.3.22.0"),sQuery(id+"F7.wireOp",EDGE,"E50.4.22.0"),sQuery(id+"F7.wireOp",EDGE,"E50.6.22.0"),sQuery(id+"F7.wireOp",EDGE,"E50.3.23.0"),sQuery(id+"F7.wireOp",EDGE,"E50.4.23.0"),sQuery(id+"F7.wireOp",EDGE,"E50.6.23.0"),sQuery(id+"F7.wireOp",EDGE,"E50.3.24.0"),sQuery(id+"F7.wireOp",EDGE,"E50.4.24.0"),sQuery(id+"F7.wireOp",EDGE,"E50.6.24.0"),sQuery(id+"F7.wireOp",EDGE,"E50.3.25.0"),sQuery(id+"F7.wireOp",EDGE,"E50.4.25.0"),sQuery(id+"F7.wireOp",EDGE,"E50.6.25.0"),sQuery(id+"F7.wireOp",EDGE,"E50.3.26.0"),sQuery(id+"F7.wireOp",EDGE,"E50.4.26.0"),sQuery(id+"F7.wireOp",EDGE,"E50.6.26.0"),sQuery(id+"F7.wireOp",EDGE,"E50.3.27.0"),sQuery(id+"F7.wireOp",EDGE,"E50.4.27.0"),sQuery(id+"F7.wireOp",EDGE,"E50.6.27.0"),sQuery(id+"F7.wireOp",EDGE,"E50.3.28.0"),sQuery(id+"F7.wireOp",EDGE,"E50.4.28.0"),sQuery(id+"F7.wireOp",EDGE,"E50.6.28.0"),sQuery(id+"F7.wireOp",EDGE,"E50.3.29.0"),sQuery(id+"F7.wireOp",EDGE,"E50.4.29.0"),sQuery(id+"F7.wireOp",EDGE,"E50.6.29.0"),sQuery(id+"F7.wireOp",EDGE,"E50.3.30.0"),sQuery(id+"F7.wireOp",EDGE,"E50.4.30.0"),sQuery(id+"F7.wireOp",EDGE,"E50.6.30.0"),sQuery(id+"F7.wireOp",EDGE,"E50.3.31.0"),sQuery(id+"F7.wireOp",EDGE,"E50.4.31.0"),sQuery(id+"F7.wireOp",EDGE,"E50.6.31.0"),sQuery(id+"F7.wireOp",EDGE,"E50.3.32.0"),sQuery(id+"F7.wireOp",EDGE,"E50.4.32.0"),sQuery(id+"F7.wireOp",EDGE,"E50.6.32.0"),sQuery(id+"F7.wireOp",EDGE,"E50.3.33.0"),sQuery(id+"F7.wireOp",EDGE,"E50.4.33.0"),sQuery(id+"F7.wireOp",EDGE,"E50.6.33.0"),sQuery(id+"F7.wireOp",EDGE,"E50.3.34.0"),sQuery(id+"F7.wireOp",EDGE,"E50.4.34.0"),sQuery(id+"F7.wireOp",EDGE,"E50.6.34.0"),sQuery(id+"F7.wireOp",EDGE,"E50.3.35.0"),sQuery(id+"F7.wireOp",EDGE,"E50.4.35.0"),sQuery(id+"F7.wireOp",EDGE,"E50.6.35.0"),sQuery(id+"F7.wireOp",EDGE,"E50.3.36.0"),sQuery(id+"F7.wireOp",EDGE,"E50.4.36.0"),sQuery(id+"F7.wireOp",EDGE,"E50.6.36.0"),sQuery(id+"F7.wireOp",EDGE,"E50.3.37.0"),sQuery(id+"F7.wireOp",EDGE,"E50.4.37.0"),sQuery(id+"F7.wireOp",EDGE,"E50.6.37.0"),sQuery(id+"F7.wireOp",EDGE,"E51")])],"isStart":false});
            var sketch = newSketch(context, id + "F9", { "sketchPlane" : qUnion([Q0])});
            skCircle(sketch, "E62", {"center": v(0, -25) * mm, "radius": 1.75 * mm});
            skSolve(sketch);
        }
        {
            var Q0;
            Q0 = qSketchRegion(id + "F9", true);
            extrude(context, id + "F10", {"entities" : qUnion([Q0]), "operationType" : NewBodyOperationType.ADD, "oppositeDirection" : true, "depth" : 12 * mm, "offsetDistance" : 25 * mm});
        }
        {
            var Q0;
            Q0=qCreatedBy(makeId("Top.planeOp"),FACE);
            var sketch = newSketch(context, id + "F11", { "sketchPlane" : qUnion([Q0])});
            skLineSegment(sketch, "E63.bottom", {"start": v(17, -17) * mm, "end": v(-17, -17) * mm});
            skLineSegment(sketch, "E63.top", {"start": v(17, 17) * mm, "end": v(-17, 17) * mm});
            skLineSegment(sketch, "E63.left", {"start": v(17, -17) * mm, "end": v(17, 17) * mm});
            skLineSegment(sketch, "E63.right", {"start": v(-17, -17) * mm, "end": v(-17, 17) * mm});
            skPoint(sketch, "E63.middle", {"position": v(0, 0) * mm});
            skSolve(sketch);
        }
        {
            var Q0;
            Q0=makeQuery(id+"F11.imprint","IMPRINT",FACE,{"disambiguationData":[TD([[makeQuery(id+"F11.imprint","IMPRINT",EDGE,{"derivedFrom":sQuery(id+"F11.wireOp",EDGE,"E63.bottom")}),-1.0]])]});
            extrude(context, id + "F12", {"entities" : qUnion([Q0]), "depth" : 3 * mm, "offsetDistance" : 25 * mm});
        }
        {
            var Q0;
            Q0=makeQuery(id+"F12.opExtrude","CAP_FACE",FACE,{"disambiguationData":[OSD([sQuery(id+"F11.wireOp",EDGE,"E63.bottom"),sQuery(id+"F11.wireOp",EDGE,"E63.top"),sQuery(id+"F11.wireOp",EDGE,"E63.left"),sQuery(id+"F11.wireOp",EDGE,"E63.right")])],"isStart":false});
            var sketch = newSketch(context, id + "F13", { "sketchPlane" : qUnion([Q0])});
            skLineSegment(sketch, "E64.bottom", {"start": v(-17, 17) * mm, "end": v(17, 17) * mm});
            skLineSegment(sketch, "E64.top", {"start": v(-17, 14) * mm, "end": v(17, 14) * mm});
            skLineSegment(sketch, "E64.left", {"start": v(-17, 17) * mm, "end": v(-17, 14) * mm});
            skLineSegment(sketch, "E64.right", {"start": v(17, 17) * mm, "end": v(17, 14) * mm});
            skSolve(sketch);
        }
        {
            var Q0;
            Q0 = qSketchRegion(id + "F13", true);
            extrude(context, id + "F14", {"entities" : qUnion([Q0]), "operationType" : NewBodyOperationType.ADD, "depth" : 32 * mm, "offsetDistance" : 25 * mm});
        }
        {
            var Q0;
            Q0=makeQuery(id+"F12.opExtrude","CAP_FACE",FACE,{"disambiguationData":[OSD([sQuery(id+"F11.wireOp",EDGE,"E63.bottom"),sQuery(id+"F11.wireOp",EDGE,"E63.top"),sQuery(id+"F11.wireOp",EDGE,"E63.left"),sQuery(id+"F11.wireOp",EDGE,"E63.right")])],"isStart":false});
            var sketch = newSketch(context, id + "F15", { "sketchPlane" : qUnion([Q0])});
            skLineSegment(sketch, "E65.bottom", {"start": v(-14, -2) * mm, "end": v(1.17, -2) * mm});
            skLineSegment(sketch, "E65.top", {"start": v(-14, -14) * mm, "end": v(1.17, -14) * mm});
            skLineSegment(sketch, "E65.left", {"start": v(-14, -2) * mm, "end": v(-14, -14) * mm});
            skLineSegment(sketch, "E65.right", {"start": v(1.17, -2) * mm, "end": v(1.17, -14) * mm});
            skLineSegment(sketch, "E66.bottom", {"start": v(-14, -2) * mm, "end": v(14, -2) * mm});
            skLineSegment(sketch, "E66.top", {"start": v(-14, 11) * mm, "end": v(14, 11) * mm});
            skLineSegment(sketch, "E66.left", {"start": v(-14, -2) * mm, "end": v(-14, 11) * mm});
            skLineSegment(sketch, "E66.right", {"start": v(14, -2) * mm, "end": v(14, 11) * mm});
            skPoint(sketch, "E66.middle", {"position": v(0, 4.5) * mm});
            skSolve(sketch);
        }
        {
            var Q0;
            Q0=makeQuery(id+"F15.imprint","IMPRINT",FACE,{"disambiguationData":[TD([[makeQuery(id+"F15.imprint","IMPRINT",EDGE,{"derivedFrom":sQuery(id+"F15.wireOp",EDGE,"E66.top")}),-1.0]])]});
            var Q1;
            Q1=makeQuery(id+"F15.imprint","IMPRINT",FACE,{"disambiguationData":[TD([[makeQuery(id+"F15.imprint","IMPRINT",EDGE,{"derivedFrom":sQuery(id+"F15.wireOp",EDGE,"E65.top")}),1.0]])]});
            extrude(context, id + "F16", {"entities" : qUnion([Q0, Q1]), "operationType" : NewBodyOperationType.REMOVE, "oppositeDirection" : true, "depth" : 25 * mm, "offsetDistance" : 25 * mm});
        }
        {
            var Q0;
            Q0=qCreatedBy(makeId("Front.planeOp"),FACE);
            var sketch = newSketch(context, id + "F17", { "sketchPlane" : qUnion([Q0])});
            skCircle(sketch, "E67", {"center": v(0, 0) * mm, "radius": 1.5 * mm});
            skCircle(sketch, "E68.0", {"center": v(0, 0) * mm, "radius": 2.5 * mm});
            skCircle(sketch, "E69.0", {"center": v(0, 0) * mm, "radius": 3.5 * mm});
            skCircle(sketch, "E70.0", {"center": v(0, 0) * mm, "radius": 4.5 * mm});
            skCircle(sketch, "E71.0", {"center": v(0, 0) * mm, "radius": 5.5 * mm});
            skCircle(sketch, "E72.0", {"center": v(0, 0) * mm, "radius": 6.5 * mm});
            skCircle(sketch, "E73.0", {"center": v(0, 0) * mm, "radius": 7.5 * mm});
            skCircle(sketch, "E74.0", {"center": v(0, 0) * mm, "radius": 2.1 * mm});
            skCircle(sketch, "E75.0", {"center": v(0, 0) * mm, "radius": 6.1 * mm});
            skCircle(sketch, "E76.0", {"center": v(0, 0) * mm, "radius": 4.1 * mm});
            skLineSegment(sketch, "E77.bottom", {"start": v(0.6, 0.6) * mm, "end": v(-0.6, 0.6) * mm});
            skLineSegment(sketch, "E77.top", {"start": v(0.6, -0.6) * mm, "end": v(-0.6, -0.6) * mm});
            skLineSegment(sketch, "E77.left", {"start": v(0.6, 0.6) * mm, "end": v(0.6, -0.6) * mm});
            skLineSegment(sketch, "E77.right", {"start": v(-0.6, 0.6) * mm, "end": v(-0.6, -0.6) * mm});
            skSolve(sketch);
        }
        {
            var Q0;
            Q0=makeQuery(id+"F17.imprint","IMPRINT",FACE,{"disambiguationData":[TD([[makeQuery(id+"F17.imprint","IMPRINT",EDGE,{"derivedFrom":sQuery(id+"F17.wireOp",EDGE,"E67")}),1.0]])]});
            var Q1;
            Q1=makeQuery(id+"F17.imprint","IMPRINT",FACE,{"disambiguationData":[TD([[makeQuery(id+"F17.imprint","IMPRINT",EDGE,{"derivedFrom":sQuery(id+"F17.wireOp",EDGE,"HSCj1mYg-onSK-Qr9o-XxYH-qQJuFH65VZT1")}),1.0]])]});
            extrude(context, id + "F18", {"entities" : qUnion([Q0, Q1]), "depth" : 34 * mm, "offsetDistance" : 25 * mm});
        }
        {
            var Q0;
            Q0=makeQuery(id+"F17.imprint","IMPRINT",FACE,{"disambiguationData":[TD([[makeQuery(id+"F17.imprint","IMPRINT",EDGE,{"derivedFrom":sQuery(id+"F17.wireOp",EDGE,"E68.0")}),-1.0]])]});
            extrude(context, id + "F19", {"entities" : qUnion([Q0]), "depth" : 32 * mm, "offsetDistance" : 25 * mm});
        }
        {
            var Q0;
            Q0=makeQuery(id+"F17.imprint","IMPRINT",FACE,{"disambiguationData":[TD([[makeQuery(id+"F17.imprint","IMPRINT",EDGE,{"derivedFrom":sQuery(id+"F17.wireOp",EDGE,"E70.0")}),-1.0]])]});
            extrude(context, id + "F20", {"entities" : qUnion([Q0]), "depth" : 34 * mm, "offsetDistance" : 25 * mm});
        }
        {
            var Q0;
            Q0=makeQuery(id+"F17.imprint","IMPRINT",FACE,{"disambiguationData":[TD([[makeQuery(id+"F17.imprint","IMPRINT",EDGE,{"derivedFrom":sQuery(id+"F17.wireOp",EDGE,"E72.0")}),-1.0]])]});
            extrude(context, id + "F21", {"entities" : qUnion([Q0]), "depth" : 34 * mm, "offsetDistance" : 25 * mm});
        }
        {
            var Q0;
            Q0=makeQuery(id+"F17.imprint","IMPRINT",FACE,{"disambiguationData":[TD([[makeQuery(id+"F17.imprint","IMPRINT",EDGE,{"derivedFrom":sQuery(id+"F17.wireOp",EDGE,"E67")}),-1.0]])]});
            extrude(context, id + "F22", {"entities" : qUnion([Q0]), "operationType" : NewBodyOperationType.ADD, "depth" : 1 * mm, "offsetDistance" : 25 * mm});
        }
        {
            var Q0;
            Q0=makeQuery(id+"F17.imprint","IMPRINT",FACE,{"disambiguationData":[TD([[makeQuery(id+"F17.imprint","IMPRINT",EDGE,{"derivedFrom":sQuery(id+"F17.wireOp",EDGE,"E69.0")}),-1.0]])]});
            var Q1;
            Q1=sQuery(id+"F17.wireOp",EDGE,"E76.0");
            extrude(context, id + "F23", {"entities" : qUnion([Q0]), "operationType" : NewBodyOperationType.ADD, "surfaceEntities" : qUnion([Q1]), "depth" : 1 * mm, "offsetDistance" : 25 * mm});
        }
        {
            var Q0;
            Q0=makeQuery(id+"F17.imprint","IMPRINT",FACE,{"disambiguationData":[TD([[makeQuery(id+"F17.imprint","IMPRINT",EDGE,{"derivedFrom":sQuery(id+"F17.wireOp",EDGE,"E71.0")}),-1.0]])]});
            extrude(context, id + "F24", {"entities" : qUnion([Q0]), "operationType" : NewBodyOperationType.ADD, "depth" : 1 * mm, "offsetDistance" : 25 * mm});
        }
        {
            var Q0;
            Q0=qCreatedBy(makeId("Right.planeOp"),FACE);
            var sketch = newSketch(context, id + "F25", { "sketchPlane" : qUnion([Q0])});
            skLineSegment(sketch, "E78.bottom", {"start": v(-33, -0.75) * mm, "end": v(-32, -0.75) * mm});
            skLineSegment(sketch, "E78.top", {"start": v(-33, 0.75) * mm, "end": v(-32, 0.75) * mm});
            skLineSegment(sketch, "E78.left", {"start": v(-33, -0.75) * mm, "end": v(-33, 0.75) * mm});
            skLineSegment(sketch, "E78.right", {"start": v(-32, -0.75) * mm, "end": v(-32, 0.75) * mm});
            skPoint(sketch, "E78.middle", {"position": v(-32.5, 0) * mm});
            skSolve(sketch);
        }
        {
            var Q0;
            Q0 = qSketchRegion(id + "F25", true);
            extrude(context, id + "F26", {"entities" : qUnion([Q0]), "operationType" : NewBodyOperationType.ADD, "oppositeDirection" : true, "depth" : 3 * mm, "offsetDistance" : 25 * mm, "hasSecondDirection" : true, "secondDirectionOppositeDirection" : true, "secondDirectionDepth" : 1.6 * mm});
        }
        {
            var Q0;
            Q0 = qSketchRegion(id + "F25", true);
            extrude(context, id + "F27", {"entities" : qUnion([Q0]), "operationType" : NewBodyOperationType.ADD, "oppositeDirection" : true, "depth" : 5 * mm, "offsetDistance" : 25 * mm, "hasSecondDirection" : true, "secondDirectionOppositeDirection" : true, "secondDirectionDepth" : 3.7 * mm});
        }
        {
            var Q0;
            Q0 = qSketchRegion(id + "F25", true);
            extrude(context, id + "F28", {"entities" : qUnion([Q0]), "operationType" : NewBodyOperationType.ADD, "oppositeDirection" : true, "depth" : 7 * mm, "offsetDistance" : 25 * mm, "hasSecondDirection" : true, "secondDirectionOppositeDirection" : true, "secondDirectionDepth" : 5.8 * mm});
        }
        {
            var Q0;
            Q0=makeQuery(id+"F12.opExtrude","SWEPT_FACE",FACE,{"disambiguationData":[OSD([sQuery(id+"F11.wireOp",EDGE,"E63.bottom")])]});
            var sketch = newSketch(context, id + "F29", { "sketchPlane" : qUnion([Q0])});
            skLineSegment(sketch, "E79.bottom", {"start": v(0.5, 1) * mm, "end": v(-0.5, 1) * mm});
            skLineSegment(sketch, "E79.top", {"start": v(0.5, 2) * mm, "end": v(-0.5, 2) * mm});
            skLineSegment(sketch, "E79.left", {"start": v(0.5, 1) * mm, "end": v(0.5, 2) * mm});
            skLineSegment(sketch, "E79.right", {"start": v(-0.5, 1) * mm, "end": v(-0.5, 2) * mm});
            skPoint(sketch, "E79.middle", {"position": v(0, 1.5) * mm});
            skCircle(sketch, "E80", {"center": v(0, 1.5) * mm, "radius": 1 * mm});
            skSolve(sketch);
        }
        {
            var Q0;
            Q0=makeQuery(id+"F12.opExtrude","CAP_FACE",FACE,{"disambiguationData":[OSD([sQuery(id+"F11.wireOp",EDGE,"E63.bottom"),sQuery(id+"F11.wireOp",EDGE,"E63.top"),sQuery(id+"F11.wireOp",EDGE,"E63.left"),sQuery(id+"F11.wireOp",EDGE,"E63.right")])],"isStart":true});
            var sketch = newSketch(context, id + "F30", { "sketchPlane" : qUnion([Q0])});
            skCircle(sketch, "E81", {"center": v(0, -16) * mm, "radius": 1 * mm});
            skLineSegment(sketch, "E82.bottom", {"start": v(-1.5, -17) * mm, "end": v(1.5, -17) * mm});
            skLineSegment(sketch, "E82.top", {"start": v(-1.5, -15) * mm, "end": v(1.5, -15) * mm});
            skLineSegment(sketch, "E82.left", {"start": v(-1.5, -17) * mm, "end": v(-1.5, -15) * mm});
            skLineSegment(sketch, "E82.right", {"start": v(1.5, -17) * mm, "end": v(1.5, -15) * mm});
            skSolve(sketch);
        }
        {
            var Q0;
            Q0=makeQuery(id+"F30.imprint","IMPRINT",FACE,{"disambiguationData":[TD([[makeQuery(id+"F30.imprint","IMPRINT",EDGE,{"derivedFrom":sQuery(id+"F30.wireOp",EDGE,"E81")}),1.0]])]});
            extrude(context, id + "F31", {"entities" : qUnion([Q0]), "operationType" : NewBodyOperationType.ADD, "depth" : 10 * mm, "offsetDistance" : 25 * mm});
        }
        {
            var Q0;
            {var subQ0=sQuery(id+"F2.wireOp",EDGE,"E34.bottom");Q0=makeQuery(id+"F5.boolean.opBoolean","MERGE",FACE,{"derivedFrom":[makeQuery(id+"F3.opExtrude","CAP_FACE",FACE,{"disambiguationData":[OSD([subQ0,sQuery(id+"F2.wireOp",EDGE,"E34.top"),sQuery(id+"F2.wireOp",EDGE,"E34.right"),sQuery(id+"F2.wireOp",EDGE,"E34.left")])],"isStart":false}),makeQuery(id+"F5.opExtrude","CAP_FACE",FACE,{"disambiguationData":[OSD([subQ0,sQuery(id+"F2.wireOp",EDGE,"E39.19.0.0"),sQuery(id+"F2.wireOp",EDGE,"E39.19.0.1"),sQuery(id+"F2.wireOp",EDGE,"E39.19.0.2")])],"isStart":false}),makeQuery(id+"F5.opExtrude","CAP_FACE",FACE,{"disambiguationData":[OSD([subQ0,sQuery(id+"F2.wireOp",EDGE,"E39.18.0.0"),sQuery(id+"F2.wireOp",EDGE,"E39.18.0.1"),sQuery(id+"F2.wireOp",EDGE,"E39.18.0.2")])],"isStart":false}),makeQuery(id+"F5.opExtrude","CAP_FACE",FACE,{"disambiguationData":[OSD([subQ0,sQuery(id+"F2.wireOp",EDGE,"E39.17.0.0"),sQuery(id+"F2.wireOp",EDGE,"E39.17.0.1"),sQuery(id+"F2.wireOp",EDGE,"E39.17.0.2")])],"isStart":false}),makeQuery(id+"F5.opExtrude","CAP_FACE",FACE,{"disambiguationData":[OSD([subQ0,sQuery(id+"F2.wireOp",EDGE,"E39.16.0.0"),sQuery(id+"F2.wireOp",EDGE,"E39.16.0.1"),sQuery(id+"F2.wireOp",EDGE,"E39.16.0.2")])],"isStart":false}),makeQuery(id+"F5.opExtrude","CAP_FACE",FACE,{"disambiguationData":[OSD([subQ0,sQuery(id+"F2.wireOp",EDGE,"E39.15.0.0"),sQuery(id+"F2.wireOp",EDGE,"E39.15.0.1"),sQuery(id+"F2.wireOp",EDGE,"E39.15.0.2")])],"isStart":false}),makeQuery(id+"F5.opExtrude","CAP_FACE",FACE,{"disambiguationData":[OSD([subQ0,sQuery(id+"F2.wireOp",EDGE,"E39.14.0.0"),sQuery(id+"F2.wireOp",EDGE,"E39.14.0.1"),sQuery(id+"F2.wireOp",EDGE,"E39.14.0.2")])],"isStart":false}),makeQuery(id+"F5.opExtrude","CAP_FACE",FACE,{"disambiguationData":[OSD([subQ0,sQuery(id+"F2.wireOp",EDGE,"E39.13.0.0"),sQuery(id+"F2.wireOp",EDGE,"E39.13.0.1"),sQuery(id+"F2.wireOp",EDGE,"E39.13.0.2")])],"isStart":false}),makeQuery(id+"F5.opExtrude","CAP_FACE",FACE,{"disambiguationData":[OSD([subQ0,sQuery(id+"F2.wireOp",EDGE,"E39.12.0.0"),sQuery(id+"F2.wireOp",EDGE,"E39.12.0.1"),sQuery(id+"F2.wireOp",EDGE,"E39.12.0.2")])],"isStart":false}),makeQuery(id+"F5.opExtrude","CAP_FACE",FACE,{"disambiguationData":[OSD([subQ0,sQuery(id+"F2.wireOp",EDGE,"E39.11.0.0"),sQuery(id+"F2.wireOp",EDGE,"E39.11.0.1"),sQuery(id+"F2.wireOp",EDGE,"E39.11.0.2")])],"isStart":false}),makeQuery(id+"F5.opExtrude","CAP_FACE",FACE,{"disambiguationData":[OSD([subQ0,sQuery(id+"F2.wireOp",EDGE,"E39.10.0.0"),sQuery(id+"F2.wireOp",EDGE,"E39.10.0.1"),sQuery(id+"F2.wireOp",EDGE,"E39.10.0.2")])],"isStart":false}),makeQuery(id+"F5.opExtrude","CAP_FACE",FACE,{"disambiguationData":[OSD([subQ0,sQuery(id+"F2.wireOp",EDGE,"E39.9.0.0"),sQuery(id+"F2.wireOp",EDGE,"E39.9.0.1"),sQuery(id+"F2.wireOp",EDGE,"E39.9.0.2")])],"isStart":false}),makeQuery(id+"F5.opExtrude","CAP_FACE",FACE,{"disambiguationData":[OSD([subQ0,sQuery(id+"F2.wireOp",EDGE,"E39.8.0.0"),sQuery(id+"F2.wireOp",EDGE,"E39.8.0.1"),sQuery(id+"F2.wireOp",EDGE,"E39.8.0.2")])],"isStart":false}),makeQuery(id+"F5.opExtrude","CAP_FACE",FACE,{"disambiguationData":[OSD([subQ0,sQuery(id+"F2.wireOp",EDGE,"E39.7.0.0"),sQuery(id+"F2.wireOp",EDGE,"E39.7.0.1"),sQuery(id+"F2.wireOp",EDGE,"E39.7.0.2")])],"isStart":false}),makeQuery(id+"F5.opExtrude","CAP_FACE",FACE,{"disambiguationData":[OSD([subQ0,sQuery(id+"F2.wireOp",EDGE,"E39.6.0.0"),sQuery(id+"F2.wireOp",EDGE,"E39.6.0.1"),sQuery(id+"F2.wireOp",EDGE,"E39.6.0.2")])],"isStart":false}),makeQuery(id+"F5.opExtrude","CAP_FACE",FACE,{"disambiguationData":[OSD([subQ0,sQuery(id+"F2.wireOp",EDGE,"E39.5.0.0"),sQuery(id+"F2.wireOp",EDGE,"E39.5.0.1"),sQuery(id+"F2.wireOp",EDGE,"E39.5.0.2")])],"isStart":false}),makeQuery(id+"F5.opExtrude","CAP_FACE",FACE,{"disambiguationData":[OSD([subQ0,sQuery(id+"F2.wireOp",EDGE,"E39.4.0.0"),sQuery(id+"F2.wireOp",EDGE,"E39.4.0.1"),sQuery(id+"F2.wireOp",EDGE,"E39.4.0.2")])],"isStart":false}),makeQuery(id+"F5.opExtrude","CAP_FACE",FACE,{"disambiguationData":[OSD([subQ0,sQuery(id+"F2.wireOp",EDGE,"E39.3.0.0"),sQuery(id+"F2.wireOp",EDGE,"E39.3.0.1"),sQuery(id+"F2.wireOp",EDGE,"E39.3.0.2")])],"isStart":false}),makeQuery(id+"F5.opExtrude","CAP_FACE",FACE,{"disambiguationData":[OSD([subQ0,sQuery(id+"F2.wireOp",EDGE,"E39.2.0.0"),sQuery(id+"F2.wireOp",EDGE,"E39.2.0.1"),sQuery(id+"F2.wireOp",EDGE,"E39.2.0.2")])],"isStart":false}),makeQuery(id+"F5.opExtrude","CAP_FACE",FACE,{"disambiguationData":[OSD([subQ0,sQuery(id+"F2.wireOp",EDGE,"E39.1.0.0"),sQuery(id+"F2.wireOp",EDGE,"E39.1.0.1"),sQuery(id+"F2.wireOp",EDGE,"E39.1.0.2")])],"isStart":false}),makeQuery(id+"F5.opExtrude","CAP_FACE",FACE,{"disambiguationData":[OSD([subQ0,sQuery(id+"F2.wireOp",EDGE,"E36"),sQuery(id+"F2.wireOp",EDGE,"E37"),sQuery(id+"F2.wireOp",EDGE,"E38")])],"isStart":false})]});}
            var sketch = newSketch(context, id + "F32", { "sketchPlane" : qUnion([Q0])});
            skCircle(sketch, "E83", {"center": v(65.5, 0) * mm, "radius": 1 * mm});
            skLineSegment(sketch, "E84.bottom", {"start": v(67.5, -4) * mm, "end": v(63.5, -4) * mm});
            skLineSegment(sketch, "E84.top", {"start": v(67.5, 4) * mm, "end": v(63.5, 4) * mm});
            skLineSegment(sketch, "E84.left", {"start": v(67.5, -4) * mm, "end": v(67.5, 4) * mm});
            skLineSegment(sketch, "E84.right", {"start": v(63.5, -4) * mm, "end": v(63.5, 4) * mm});
            skLineSegment(sketch, "E85.bottom", {"start": v(67.5, 4) * mm, "end": v(61.5, 4) * mm});
            skLineSegment(sketch, "E85.top", {"start": v(67.5, 10) * mm, "end": v(61.5, 10) * mm});
            skLineSegment(sketch, "E85.left", {"start": v(67.5, 4) * mm, "end": v(67.5, 10) * mm});
            skLineSegment(sketch, "E85.right", {"start": v(61.5, 4) * mm, "end": v(61.5, 10) * mm});
            skCircle(sketch, "E86", {"center": v(64.5, 7) * mm, "radius": 1.06 * mm});
            skPoint(sketch, "E86.centerSnap0", {"position": v(61.5, 7) * mm});
            skPoint(sketch, "E86.centerSnap1", {"position": v(64.5, 10) * mm});
            skSolve(sketch);
        }
        {
            var Q0;
            Q0=makeQuery(id+"F32.imprint","IMPRINT",FACE,{"disambiguationData":[TD([[makeQuery(id+"F32.imprint","IMPRINT",EDGE,{"derivedFrom":sQuery(id+"F32.wireOp",EDGE,"E85.top")}),1.0]])]});
            extrude(context, id + "F33", {"entities" : qUnion([Q0]), "operationType" : NewBodyOperationType.ADD, "oppositeDirection" : true, "depth" : 4 * mm, "offsetDistance" : 25 * mm});
        }
        {
            var Q0;
            Q0=qCreatedBy(makeId("Top.planeOp"),FACE);
            var sketch = newSketch(context, id + "F34", { "sketchPlane" : qUnion([Q0])});
            skCircle(sketch, "E87", {"center": v(0, -5) * mm, "radius": 2.5 * mm});
            skSolve(sketch);
        }
        {
            var Q0;
            Q0 = qSketchRegion(id + "F34", true);
            extrude(context, id + "F35", {"entities" : qUnion([Q0]), "operationType" : NewBodyOperationType.REMOVE, "oppositeDirection" : true, "depth" : 10.1 * mm, "offsetDistance" : 25 * mm, "hasSecondDirection" : true, "secondDirectionOppositeDirection" : false, "secondDirectionDepth" : 36.7 * mm});
        }
        {
            var Q0;
            Q0=makeQuery(id+"F14.boolean.opBoolean","MERGE",FACE,{"derivedFrom":[makeQuery(id+"F12.opExtrude","SWEPT_FACE",FACE,{"disambiguationData":[OSD([sQuery(id+"F11.wireOp",EDGE,"E63.top")])]}),makeQuery(id+"F14.opExtrude","SWEPT_FACE",FACE,{"disambiguationData":[OSD([sQuery(id+"F13.wireOp",EDGE,"E64.bottom")])]})]});
            var sketch = newSketch(context, id + "F36", { "sketchPlane" : qUnion([Q0])});
            skCircle(sketch, "E88", {"center": v(-12, 31) * mm, "radius": 2.05 * mm});
            skCircle(sketch, "E89", {"center": v(12, 31) * mm, "radius": 1.68 * mm});
            skCircle(sketch, "E90", {"center": v(-12, 6) * mm, "radius": 1.64 * mm});
            skCircle(sketch, "E91", {"center": v(12, 6) * mm, "radius": 1.9 * mm});
            skLineSegment(sketch, "E92.bottom", {"start": v(1.5, 3) * mm, "end": v(-1.5, 3) * mm});
            skLineSegment(sketch, "E92.top", {"start": v(1.5, 6) * mm, "end": v(-1.5, 6) * mm});
            skLineSegment(sketch, "E92.left", {"start": v(1.5, 3) * mm, "end": v(1.5, 6) * mm});
            skLineSegment(sketch, "E92.right", {"start": v(-1.5, 3) * mm, "end": v(-1.5, 6) * mm});
            skPoint(sketch, "E92.middle", {"position": v(0, 4.5) * mm});
            skSolve(sketch);
        }
        {
            var Q0;
            Q0=sQuery(id+"F36.wireOp",VERTEX,"E88.center");
            var Q1;
            Q1=sQuery(id+"F36.wireOp",VERTEX,"E89.center");
            var Q2;
            Q2=sQuery(id+"F36.wireOp",VERTEX,"E91.center");
            var Q3;
            Q3=sQuery(id+"F36.wireOp",VERTEX,"E90.center");
            var Q4;
            Q4=makeQuery(id+"F12.opExtrude","SWEPT_BODY",BODY,{"disambiguationData":[OSD([sQuery(id+"F11.wireOp",EDGE,"E63.bottom"),sQuery(id+"F11.wireOp",EDGE,"E63.top"),sQuery(id+"F11.wireOp",EDGE,"E63.left"),sQuery(id+"F11.wireOp",EDGE,"E63.right")])]});
            hole(context, id + "F37", {"style" : HoleStyle.C_BORE, "endStyle" : HoleEndStyle.BLIND, "holeDiameter" : 3.5 * mm, "cBoreDiameter" : 6.5 * mm, "cBoreDepth" : 1.5 * mm, "majorDiameter" : 5 * mm, "holeDepth" : 12 * mm, "isTappedThrough" : true, "tappedDepth" : 12 * mm, "tapClearance" : 3, "locations" : qUnion([Q0, Q1, Q2, Q3]), "scope" : qUnion([Q4])});
        }
        {
            var Q0;
            Q0=qCreatedBy(makeId("Right.planeOp"),FACE);
            var sketch = newSketch(context, id + "F38", { "sketchPlane" : qUnion([Q0])});
            skLineSegment(sketch, "E93", {"start": v(-1, -6) * mm, "end": v(-3, -6) * mm});
            skLineSegment(sketch, "E94", {"start": v(3, -6) * mm, "end": v(1, -6) * mm});
            skLineSegment(sketch, "E95", {"start": v(-1, -8) * mm, "end": v(-2, -8) * mm});
            skLineSegment(sketch, "E96", {"start": v(1, -8) * mm, "end": v(2, -8) * mm});
            skLineSegment(sketch, "E97", {"start": v(-1, -6) * mm, "end": v(-1, -8) * mm});
            skLineSegment(sketch, "E98", {"start": v(-2, -8) * mm, "end": v(-3, -6) * mm});
            skLineSegment(sketch, "E99", {"start": v(1, -6) * mm, "end": v(1, -8) * mm});
            skLineSegment(sketch, "E100", {"start": v(2, -8) * mm, "end": v(3, -6) * mm});
            skSolve(sketch);
        }
        {
            var Q0;
            Q0=makeQuery(id+"F38.imprint","IMPRINT",FACE,{"disambiguationData":[TD([[makeQuery(id+"F38.imprint","IMPRINT",EDGE,{"derivedFrom":sQuery(id+"F38.wireOp",EDGE,"E93")}),1.0]])]});
            var Q1;
            Q1=sQuery(id+"F38.wireOp",EDGE,"E97");
            revolve(context, id + "F39", {"operationType" : NewBodyOperationType.ADD, "entities" : qUnion([Q0]), "axis" : qUnion([Q1]), "revolveType" : RevolveType.SYMMETRIC, "angle" : 180 * degree});
        }
        {
            var Q0;
            Q0=makeQuery(id+"F38.imprint","IMPRINT",FACE,{"disambiguationData":[TD([[makeQuery(id+"F38.imprint","IMPRINT",EDGE,{"derivedFrom":sQuery(id+"F38.wireOp",EDGE,"E94")}),1.0]])]});
            var Q1;
            Q1=sQuery(id+"F38.wireOp",EDGE,"E99");
            revolve(context, id + "F40", {"operationType" : NewBodyOperationType.ADD, "entities" : qUnion([Q0]), "axis" : qUnion([Q1]), "revolveType" : RevolveType.SYMMETRIC, "angle" : 180 * degree});
        }
        {
            var Q0;
            Q0=makeQuery(id+"F18.opExtrude","CAP_FACE",FACE,{"disambiguationData":[OSD([sQuery(id+"F17.wireOp",EDGE,"E67"),sQuery(id+"F17.wireOp",EDGE,"E77.bottom"),sQuery(id+"F17.wireOp",EDGE,"E77.top"),sQuery(id+"F17.wireOp",EDGE,"E77.left"),sQuery(id+"F17.wireOp",EDGE,"E77.right")])],"isStart":false});
            var sketch = newSketch(context, id + "F41", { "sketchPlane" : qUnion([Q0])});
            skLineSegment(sketch, "E101.bottom", {"start": v(1.52, -1.5) * mm, "end": v(-1.52, -1.5) * mm});
            skLineSegment(sketch, "E101.top", {"start": v(1.52, 1.5) * mm, "end": v(-1.52, 1.5) * mm});
            skLineSegment(sketch, "E101.left", {"start": v(1.52, -1.5) * mm, "end": v(1.52, 1.5) * mm});
            skLineSegment(sketch, "E101.right", {"start": v(-1.52, -1.5) * mm, "end": v(-1.52, 1.5) * mm});
            skPoint(sketch, "E101.middle", {"position": v(0, 0) * mm});
            skSolve(sketch);
        }
        {
            var Q0;
            Q0=makeQuery(id+"F41.imprint","IMPRINT",FACE,{"disambiguationData":[TD([[makeQuery(id+"F41.imprint","IMPRINT",EDGE,{"derivedFrom":makeQuery(id+"F18.opExtrude","CAP_EDGE",EDGE,{"disambiguationData":[OSD([sQuery(id+"F17.wireOp",EDGE,"E77.bottom")])],"isStart":false})}),-1.0]])]});
            var Q1;
            {var subQ0=sQuery(id+"F41.wireOp",EDGE,"E101.right");Q1=makeQuery(id+"F41.imprint","IMPRINT",FACE,{"disambiguationData":[TD([[makeQuery(id+"F41.imprint","IMPRINT",EDGE,{"derivedFrom":subQ0}),-1.0]])]});}
            var Q2;
            {var subQ0=sQuery(id+"F41.wireOp",EDGE,"E101.right");Q2=makeQuery(id+"F41.imprint","IMPRINT",FACE,{"disambiguationData":[TD([[makeQuery(id+"F41.imprint","IMPRINT",EDGE,{"derivedFrom":subQ0}),-1.0]])]});}
            var Q3;
            {var subQ0=sQuery(id+"F41.wireOp",EDGE,"E101.left");Q3=makeQuery(id+"F41.imprint","IMPRINT",FACE,{"disambiguationData":[TD([[makeQuery(id+"F41.imprint","IMPRINT",EDGE,{"derivedFrom":subQ0}),1.0]])]});}
            extrude(context, id + "F42", {"entities" : qUnion([Q0, Q1, Q2, Q3]), "operationType" : NewBodyOperationType.ADD, "depth" : 3 * mm, "offsetDistance" : 25 * mm});
        }
        {
            var Q0;
            Q0=makeQuery(id+"F36.imprint","IMPRINT",FACE,{"disambiguationData":[TD([[makeQuery(id+"F36.imprint","IMPRINT",EDGE,{"derivedFrom":sQuery(id+"F36.wireOp",EDGE,"E92.bottom")}),-1.0]])]});
            extrude(context, id + "F43", {"entities" : qUnion([Q0]), "operationType" : NewBodyOperationType.REMOVE, "oppositeDirection" : true, "depth" : 25 * mm, "offsetDistance" : 25 * mm});
        }
        {
            var Q0;
            {var subQ0=sQuery(id+"F2.wireOp",EDGE,"E34.bottom");Q0=makeQuery(id+"F5.boolean.opBoolean","MERGE",FACE,{"derivedFrom":[makeQuery(id+"F3.opExtrude","CAP_FACE",FACE,{"disambiguationData":[OSD([subQ0,sQuery(id+"F2.wireOp",EDGE,"E34.top"),sQuery(id+"F2.wireOp",EDGE,"E34.right"),sQuery(id+"F2.wireOp",EDGE,"E34.left")])],"isStart":false}),makeQuery(id+"F5.opExtrude","CAP_FACE",FACE,{"disambiguationData":[OSD([subQ0,sQuery(id+"F2.wireOp",EDGE,"E40.0.21.0"),sQuery(id+"F2.wireOp",EDGE,"E40.3.21.0"),sQuery(id+"F2.wireOp",EDGE,"E40.6.21.0")])],"isStart":false}),makeQuery(id+"F5.opExtrude","CAP_FACE",FACE,{"disambiguationData":[OSD([subQ0,sQuery(id+"F2.wireOp",EDGE,"E40.0.20.0"),sQuery(id+"F2.wireOp",EDGE,"E40.3.20.0"),sQuery(id+"F2.wireOp",EDGE,"E40.6.20.0")])],"isStart":false}),makeQuery(id+"F5.opExtrude","CAP_FACE",FACE,{"disambiguationData":[OSD([subQ0,sQuery(id+"F2.wireOp",EDGE,"E39.19.0.0"),sQuery(id+"F2.wireOp",EDGE,"E39.19.0.1"),sQuery(id+"F2.wireOp",EDGE,"E39.19.0.2")])],"isStart":false}),makeQuery(id+"F5.opExtrude","CAP_FACE",FACE,{"disambiguationData":[OSD([subQ0,sQuery(id+"F2.wireOp",EDGE,"E39.18.0.0"),sQuery(id+"F2.wireOp",EDGE,"E39.18.0.1"),sQuery(id+"F2.wireOp",EDGE,"E39.18.0.2")])],"isStart":false}),makeQuery(id+"F5.opExtrude","CAP_FACE",FACE,{"disambiguationData":[OSD([subQ0,sQuery(id+"F2.wireOp",EDGE,"E39.17.0.0"),sQuery(id+"F2.wireOp",EDGE,"E39.17.0.1"),sQuery(id+"F2.wireOp",EDGE,"E39.17.0.2")])],"isStart":false}),makeQuery(id+"F5.opExtrude","CAP_FACE",FACE,{"disambiguationData":[OSD([subQ0,sQuery(id+"F2.wireOp",EDGE,"E39.16.0.0"),sQuery(id+"F2.wireOp",EDGE,"E39.16.0.1"),sQuery(id+"F2.wireOp",EDGE,"E39.16.0.2")])],"isStart":false}),makeQuery(id+"F5.opExtrude","CAP_FACE",FACE,{"disambiguationData":[OSD([subQ0,sQuery(id+"F2.wireOp",EDGE,"E39.15.0.0"),sQuery(id+"F2.wireOp",EDGE,"E39.15.0.1"),sQuery(id+"F2.wireOp",EDGE,"E39.15.0.2")])],"isStart":false}),makeQuery(id+"F5.opExtrude","CAP_FACE",FACE,{"disambiguationData":[OSD([subQ0,sQuery(id+"F2.wireOp",EDGE,"E39.14.0.0"),sQuery(id+"F2.wireOp",EDGE,"E39.14.0.1"),sQuery(id+"F2.wireOp",EDGE,"E39.14.0.2")])],"isStart":false}),makeQuery(id+"F5.opExtrude","CAP_FACE",FACE,{"disambiguationData":[OSD([subQ0,sQuery(id+"F2.wireOp",EDGE,"E39.13.0.0"),sQuery(id+"F2.wireOp",EDGE,"E39.13.0.1"),sQuery(id+"F2.wireOp",EDGE,"E39.13.0.2")])],"isStart":false}),makeQuery(id+"F5.opExtrude","CAP_FACE",FACE,{"disambiguationData":[OSD([subQ0,sQuery(id+"F2.wireOp",EDGE,"E39.12.0.0"),sQuery(id+"F2.wireOp",EDGE,"E39.12.0.1"),sQuery(id+"F2.wireOp",EDGE,"E39.12.0.2")])],"isStart":false}),makeQuery(id+"F5.opExtrude","CAP_FACE",FACE,{"disambiguationData":[OSD([subQ0,sQuery(id+"F2.wireOp",EDGE,"E39.11.0.0"),sQuery(id+"F2.wireOp",EDGE,"E39.11.0.1"),sQuery(id+"F2.wireOp",EDGE,"E39.11.0.2")])],"isStart":false}),makeQuery(id+"F5.opExtrude","CAP_FACE",FACE,{"disambiguationData":[OSD([subQ0,sQuery(id+"F2.wireOp",EDGE,"E39.10.0.0"),sQuery(id+"F2.wireOp",EDGE,"E39.10.0.1"),sQuery(id+"F2.wireOp",EDGE,"E39.10.0.2")])],"isStart":false}),makeQuery(id+"F5.opExtrude","CAP_FACE",FACE,{"disambiguationData":[OSD([subQ0,sQuery(id+"F2.wireOp",EDGE,"E39.9.0.0"),sQuery(id+"F2.wireOp",EDGE,"E39.9.0.1"),sQuery(id+"F2.wireOp",EDGE,"E39.9.0.2")])],"isStart":false}),makeQuery(id+"F5.opExtrude","CAP_FACE",FACE,{"disambiguationData":[OSD([subQ0,sQuery(id+"F2.wireOp",EDGE,"E39.8.0.0"),sQuery(id+"F2.wireOp",EDGE,"E39.8.0.1"),sQuery(id+"F2.wireOp",EDGE,"E39.8.0.2")])],"isStart":false}),makeQuery(id+"F5.opExtrude","CAP_FACE",FACE,{"disambiguationData":[OSD([subQ0,sQuery(id+"F2.wireOp",EDGE,"E39.7.0.0"),sQuery(id+"F2.wireOp",EDGE,"E39.7.0.1"),sQuery(id+"F2.wireOp",EDGE,"E39.7.0.2")])],"isStart":false}),makeQuery(id+"F5.opExtrude","CAP_FACE",FACE,{"disambiguationData":[OSD([subQ0,sQuery(id+"F2.wireOp",EDGE,"E39.6.0.0"),sQuery(id+"F2.wireOp",EDGE,"E39.6.0.1"),sQuery(id+"F2.wireOp",EDGE,"E39.6.0.2")])],"isStart":false}),makeQuery(id+"F5.opExtrude","CAP_FACE",FACE,{"disambiguationData":[OSD([subQ0,sQuery(id+"F2.wireOp",EDGE,"E39.5.0.0"),sQuery(id+"F2.wireOp",EDGE,"E39.5.0.1"),sQuery(id+"F2.wireOp",EDGE,"E39.5.0.2")])],"isStart":false}),makeQuery(id+"F5.opExtrude","CAP_FACE",FACE,{"disambiguationData":[OSD([subQ0,sQuery(id+"F2.wireOp",EDGE,"E39.4.0.0"),sQuery(id+"F2.wireOp",EDGE,"E39.4.0.1"),sQuery(id+"F2.wireOp",EDGE,"E39.4.0.2")])],"isStart":false}),makeQuery(id+"F5.opExtrude","CAP_FACE",FACE,{"disambiguationData":[OSD([subQ0,sQuery(id+"F2.wireOp",EDGE,"E39.3.0.0"),sQuery(id+"F2.wireOp",EDGE,"E39.3.0.1"),sQuery(id+"F2.wireOp",EDGE,"E39.3.0.2")])],"isStart":false}),makeQuery(id+"F5.opExtrude","CAP_FACE",FACE,{"disambiguationData":[OSD([subQ0,sQuery(id+"F2.wireOp",EDGE,"E39.2.0.0"),sQuery(id+"F2.wireOp",EDGE,"E39.2.0.1"),sQuery(id+"F2.wireOp",EDGE,"E39.2.0.2")])],"isStart":false}),makeQuery(id+"F5.opExtrude","CAP_FACE",FACE,{"disambiguationData":[OSD([subQ0,sQuery(id+"F2.wireOp",EDGE,"E39.1.0.0"),sQuery(id+"F2.wireOp",EDGE,"E39.1.0.1"),sQuery(id+"F2.wireOp",EDGE,"E39.1.0.2")])],"isStart":false}),makeQuery(id+"F5.opExtrude","CAP_FACE",FACE,{"disambiguationData":[OSD([subQ0,sQuery(id+"F2.wireOp",EDGE,"E36"),sQuery(id+"F2.wireOp",EDGE,"E37"),sQuery(id+"F2.wireOp",EDGE,"E38")])],"isStart":false})]});}
            var sketch = newSketch(context, id + "F44", { "sketchPlane" : qUnion([Q0])});
            skText(sketch, "E102", { "text": "0               V               X              XV            XX", "fontName": "AllertaStencil-Regular.ttf"});
            const initialGuessF44  = {"E102": [-0.06508, -0.00249, 1, 0, 0.00479]};
            skSetInitialGuess(sketch, initialGuessF44);
            skSolve(sketch);
        }
        {
            var Q0;
            Q0 = qSketchRegion(id + "F44", true);
            extrude(context, id + "F45", {"entities" : qUnion([Q0]), "operationType" : NewBodyOperationType.REMOVE, "oppositeDirection" : true, "depth" : 2 * mm, "offsetDistance" : 25 * mm});
        }
        {
            var Q0;
            {var subQ5=sQuery(id+"F30.wireOp",EDGE,"E82.right");Q0=makeQuery(id+"F30.imprint","IMPRINT",FACE,{"disambiguationData":[TD([[makeQuery(id+"F30.imprint","IMPRINT",EDGE,{"derivedFrom":subQ5}),1.0]])]});}
            var Q1;
            {var subQ5=sQuery(id+"F30.wireOp",EDGE,"E82.left");Q1=makeQuery(id+"F30.imprint","IMPRINT",FACE,{"disambiguationData":[TD([[makeQuery(id+"F30.imprint","IMPRINT",EDGE,{"derivedFrom":subQ5}),-1.0]])]});}
            extrude(context, id + "F46", {"entities" : qUnion([Q0, Q1]), "operationType" : NewBodyOperationType.ADD, "depth" : 5 * mm, "offsetDistance" : 25 * mm, "hasSecondDirection" : true, "secondDirectionOppositeDirection" : false, "secondDirectionDepth" : 4 * mm});
        }
    });
